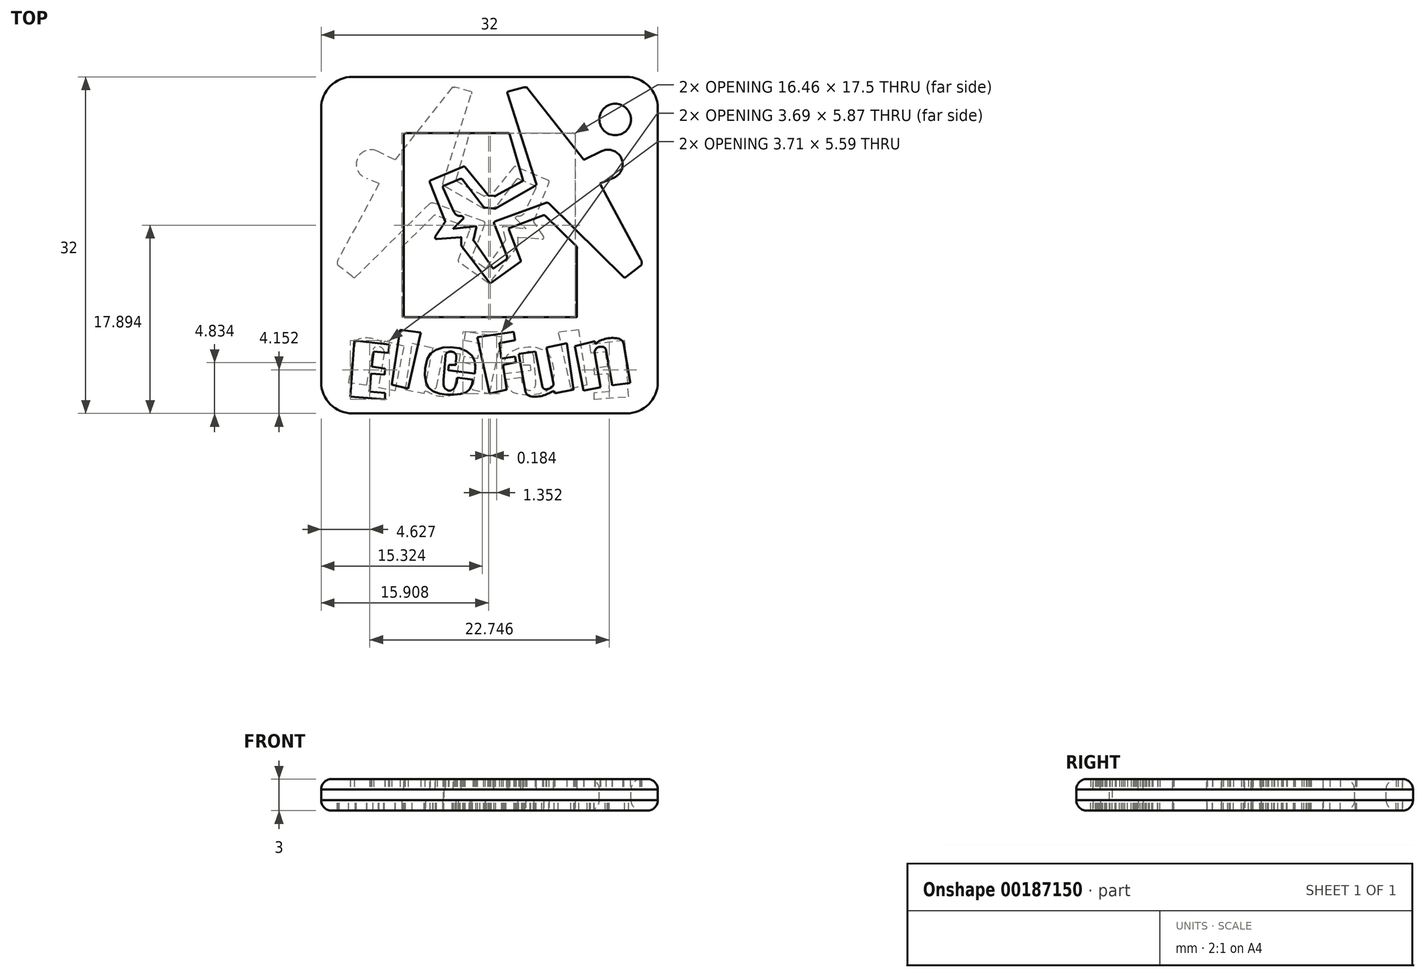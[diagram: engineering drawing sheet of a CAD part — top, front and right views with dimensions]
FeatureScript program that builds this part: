
annotation { "Feature Type Name" : "Feature", "Feature Type Description" : "" }
export const myFeature = defineFeature(function(context is Context, id is Id, definition is map)
    precondition{}
    {
        {
            var Q0;
            Q0=qCreatedBy(makeId("Top.planeOp"),FACE);
            var sketch = newSketch(context, id + "F0", { "sketchPlane" : qUnion([Q0])});
            skLineSegment(sketch, "E0", {"start": v(-15, 0) * mm, "end": v(15, 0) * mm, "construction": true});
            skLineSegment(sketch, "E1", {"start": v(0, 15) * mm, "end": v(0, 0) * mm, "construction": true});
            skLineSegment(sketch, "E2", {"start": v(0, 0) * mm, "end": v(0, -15) * mm, "construction": true});
            skLineSegment(sketch, "E3", {"start": v(1.86, 10.64) * mm, "end": v(-7.86, 10.64) * mm});
            skLineSegment(sketch, "E4", {"start": v(-8.14, 10.51) * mm, "end": v(-8.14, -6.7) * mm});
            skLineSegment(sketch, "E5", {"start": v(-8.02, -6.86) * mm, "end": v(8.23, -6.86) * mm});
            skLineSegment(sketch, "E6", {"start": v(8.32, -6.77) * mm, "end": v(8.32, -0.32) * mm});
            skLineSegment(sketch, "E7", {"start": v(8.28, -0.12) * mm, "end": v(5.28, 2.8) * mm});
            skLineSegment(sketch, "E8", {"start": v(1.92, 1.65) * mm, "end": v(5.12, 2.84) * mm});
            skLineSegment(sketch, "E9", {"start": v(1.74, 14.6) * mm, "end": v(3.24, 15) * mm});
            skLineSegment(sketch, "E10", {"start": v(3.55, 15) * mm, "end": v(8.98, 8.11) * mm});
            skLineSegment(sketch, "E11", {"start": v(8.98, 8.11) * mm, "end": v(10.65, 8.93) * mm});
            skLineSegment(sketch, "E12", {"start": v(10.49, 5.85) * mm, "end": v(11.64, 6.34) * mm});
            skLineSegment(sketch, "E13", {"start": v(10.49, 5.85) * mm, "end": v(14.37, -1.36) * mm});
            skLineSegment(sketch, "E14", {"start": v(13, -3.01) * mm, "end": v(14.27, -2.02) * mm});
            skLineSegment(sketch, "E15", {"start": v(12.74, -3.04) * mm, "end": v(5.65, 3.98) * mm});
            skLineSegment(sketch, "E16", {"start": v(0.54, 2.26) * mm, "end": v(5.35, 4.02) * mm});
            skLineSegment(sketch, "E17", {"start": v(0.45, 2.02) * mm, "end": v(1.66, -1.06) * mm});
            skLineSegment(sketch, "E18", {"start": v(2.97, -1.46) * mm, "end": v(1.87, 1.45) * mm});
            skLineSegment(sketch, "E19", {"start": v(0.4, -2.2) * mm, "end": v(1.6, -1.35) * mm});
            skLineSegment(sketch, "E20", {"start": v(0.28, -2.17) * mm, "end": v(-1.46, 0.35) * mm});
            skLineSegment(sketch, "E21", {"start": v(-1.52, 0.54) * mm, "end": v(-1.27, 1.67) * mm});
            skLineSegment(sketch, "E22", {"start": v(-1.33, 1.8) * mm, "end": v(-3.35, 1.58) * mm});
            skLineSegment(sketch, "E23", {"start": v(-2.43, 2.57) * mm, "end": v(-3.32, 1.7) * mm});
            skLineSegment(sketch, "E24", {"start": v(-2.43, 2.57) * mm, "end": v(-2.63, 2.76) * mm});
            skLineSegment(sketch, "E25", {"start": v(-4.4, 5.43) * mm, "end": v(-3.37, 3.16) * mm});
            skLineSegment(sketch, "E26", {"start": v(-2.79, 0.76) * mm, "end": v(-4.98, 0.6) * mm});
            skLineSegment(sketch, "E27", {"start": v(-5.16, 0.8) * mm, "end": v(-4.24, 2.18) * mm});
            skLineSegment(sketch, "E28", {"start": v(-4.24, 2.33) * mm, "end": v(-5.63, 5.88) * mm});
            skLineSegment(sketch, "E29", {"start": v(-5.63, 6.15) * mm, "end": v(-2.51, 7.46) * mm});
            skLineSegment(sketch, "E30", {"start": v(-2.34, 7.46) * mm, "end": v(-0.18, 4.8) * mm});
            skLineSegment(sketch, "E31", {"start": v(-0.07, 4.7) * mm, "end": v(0.46, 4.67) * mm});
            skLineSegment(sketch, "E32", {"start": v(0.57, 4.67) * mm, "end": v(3.12, 6.06) * mm});
            skLineSegment(sketch, "E33", {"start": v(3.16, 6.27) * mm, "end": v(1.9, 10.52) * mm});
            skLineSegment(sketch, "E34", {"start": v(0.1, -3.6) * mm, "end": v(2.9, -1.6) * mm});
            skLineSegment(sketch, "E35", {"start": v(-2.68, 0.7) * mm, "end": v(-2.7, 0.01) * mm});
            skLineSegment(sketch, "E36", {"start": v(-2.68, -0.05) * mm, "end": v(-0.03, -3.54) * mm});
            skLineSegment(sketch, "E37", {"start": v(-2.76, 6.3) * mm, "end": v(-4.36, 5.63) * mm});
            skLineSegment(sketch, "E38", {"start": v(-2.58, 6.26) * mm, "end": v(-0.6, 3.66) * mm});
            skLineSegment(sketch, "E39", {"start": v(-0.42, 3.58) * mm, "end": v(0.4, 3.49) * mm});
            skLineSegment(sketch, "E40", {"start": v(0.57, 3.49) * mm, "end": v(4.32, 5.63) * mm});
            skLineSegment(sketch, "E41", {"start": v(4.44, 5.9) * mm, "end": v(1.72, 14.38) * mm});
            skArc(sketch, "E42", {"start": v(11.64, 6.34) * mm, "mid": v(12.57, 8.18) * mm, "end": v(10.65, 8.93) * mm});
            skFitSpline(sketch, "E43", {"points": [v(1.74, 14.6) * mm, v(1.69, 14.5) * mm, v(1.72, 14.38) * mm], "startDerivative": vector(-0.14, -0.18) * mm, "endDerivative": vector(0.1, -0.25) * mm});
            skFitSpline(sketch, "E44", {"points": [v(3.24, 15) * mm, v(3.45, 15) * mm, v(3.55, 15) * mm], "startDerivative": vector(0.4, 0.05) * mm, "endDerivative": vector(0.21, -0.06) * mm});
            skFitSpline(sketch, "E45", {"points": [v(14.37, -1.36) * mm, v(14.45, -1.51) * mm, v(14.47, -1.68) * mm, v(14.44, -1.84) * mm, v(14.27, -2.02) * mm], "startDerivative": vector(0.37, -0.61) * mm, "endDerivative": vector(-0.7, -0.58) * mm});
            skFitSpline(sketch, "E46", {"points": [v(13, -3.01) * mm, v(12.88, -3.08) * mm, v(12.74, -3.04) * mm], "startDerivative": vector(-0.22, -0.18) * mm, "endDerivative": vector(-0.3, 0.12) * mm});
            skFitSpline(sketch, "E47", {"points": [v(5.65, 3.98) * mm, v(5.5, 4.03) * mm, v(5.35, 4.02) * mm], "startDerivative": vector(-0.3, 0.13) * mm, "endDerivative": vector(-0.3, -0.04) * mm});
            skArc(sketch, "E48", {"start": v(5.28, 2.8) * mm, "mid": v(5.2, 2.84) * mm, "end": v(5.12, 2.84) * mm});
            skFitSpline(sketch, "E49", {"points": [v(1.92, 1.65) * mm, v(1.86, 1.6) * mm, v(1.85, 1.55) * mm, v(1.87, 1.45) * mm], "startDerivative": vector(-0.21, -0.1) * mm, "endDerivative": vector(0.08, -0.26) * mm});
            skFitSpline(sketch, "E50", {"points": [v(2.97, -1.46) * mm, v(2.98, -1.5) * mm, v(2.97, -1.54) * mm, v(2.95, -1.57) * mm, v(2.9, -1.6) * mm], "startDerivative": vector(0.05, -0.15) * mm, "endDerivative": vector(-0.18, -0.1) * mm});
            skFitSpline(sketch, "E51", {"points": [v(1.66, -1.06) * mm, v(1.66, -1.2) * mm, v(1.6, -1.35) * mm], "startDerivative": vector(0.05, -0.3) * mm, "endDerivative": vector(-0.15, -0.27) * mm});
            skFitSpline(sketch, "E52", {"points": [v(0.4, -2.2) * mm, v(0.35, -2.2) * mm, v(0.28, -2.17) * mm], "startDerivative": vector(-0.13, -0.01) * mm, "endDerivative": vector(-0.12, 0.07) * mm});
            skArc(sketch, "E53", {"start": v(-1.52, 0.54) * mm, "mid": v(-1.52, 0.44) * mm, "end": v(-1.46, 0.35) * mm});
            skFitSpline(sketch, "E54", {"points": [v(-1.27, 1.67) * mm, v(-1.26, 1.7) * mm, v(-1.26, 1.75) * mm, v(-1.27, 1.77) * mm, v(-1.28, 1.79) * mm, v(-1.3, 1.8) * mm, v(-1.33, 1.8) * mm], "startDerivative": vector(0.06, 0.2) * mm, "endDerivative": vector(-0.18, -0.02) * mm});
            skFitSpline(sketch, "E55", {"points": [v(-3.32, 1.7) * mm, v(-3.4, 1.63) * mm, v(-3.44, 1.58) * mm, v(-3.43, 1.57) * mm, v(-3.4, 1.57) * mm, v(-3.35, 1.58) * mm], "startDerivative": vector(-0.28, -0.26) * mm, "endDerivative": vector(0.25, 0.03) * mm});
            skFitSpline(sketch, "E56", {"points": [v(-4.24, 2.18) * mm, v(-4.23, 2.2) * mm, v(-4.21, 2.23) * mm, v(-4.21, 2.25) * mm, v(-4.22, 2.28) * mm, v(-4.23, 2.31) * mm, v(-4.24, 2.33) * mm], "startDerivative": vector(0.05, 0.12) * mm, "endDerivative": vector(-0.05, 0.14) * mm});
            skFitSpline(sketch, "E57", {"points": [v(-2.63, 2.76) * mm, v(-2.75, 2.76) * mm, v(-2.87, 2.76) * mm, v(-3, 2.8) * mm, v(-3.15, 2.89) * mm, v(-3.26, 3) * mm, v(-3.37, 3.16) * mm], "startDerivative": vector(-0.82, 0.01) * mm, "endDerivative": vector(-0.6, 0.94) * mm});
            skFitSpline(sketch, "E58", {"points": [v(-4.4, 5.43) * mm, v(-4.44, 5.55) * mm, v(-4.36, 5.63) * mm], "startDerivative": vector(-0.14, 0.26) * mm, "endDerivative": vector(0.23, 0.16) * mm});
            skFitSpline(sketch, "E59", {"points": [v(-2.76, 6.3) * mm, v(-2.66, 6.3) * mm, v(-2.58, 6.26) * mm], "startDerivative": vector(0.22, 0.03) * mm, "endDerivative": vector(0.16, -0.12) * mm});
            skFitSpline(sketch, "E60", {"points": [v(-0.6, 3.66) * mm, v(-0.52, 3.6) * mm, v(-0.42, 3.58) * mm], "startDerivative": vector(0.15, -0.13) * mm, "endDerivative": vector(0.2, -0.02) * mm});
            skFitSpline(sketch, "E61", {"points": [v(0.4, 3.49) * mm, v(0.5, 3.49) * mm, v(0.57, 3.49) * mm], "startDerivative": vector(0.17, 0) * mm, "endDerivative": vector(0.15, 0) * mm});
            skFitSpline(sketch, "E62", {"points": [v(0.57, 4.67) * mm, v(0.54, 4.66) * mm, v(0.46, 4.67) * mm], "startDerivative": vector(-0.06, -0.02) * mm, "endDerivative": vector(-0.15, 0.02) * mm});
            skFitSpline(sketch, "E63", {"points": [v(-0.07, 4.7) * mm, v(-0.12, 4.73) * mm, v(-0.18, 4.8) * mm], "startDerivative": vector(-0.12, 0.05) * mm, "endDerivative": vector(-0.1, 0.13) * mm});
            skFitSpline(sketch, "E64", {"points": [v(-8.14, 10.51) * mm, v(-8.07, 10.6) * mm, v(-7.95, 10.64) * mm, v(-7.86, 10.64) * mm], "startDerivative": vector(0.18, 0.27) * mm, "endDerivative": vector(0.29, 0) * mm});
            skFitSpline(sketch, "E65", {"points": [v(1.9, 10.52) * mm, v(1.88, 10.6) * mm, v(1.86, 10.64) * mm], "startDerivative": vector(-0.05, 0.15) * mm, "endDerivative": vector(-0.04, 0.1) * mm});
            skFitSpline(sketch, "E66", {"points": [v(4.44, 5.9) * mm, v(4.45, 5.84) * mm, v(4.45, 5.77) * mm, v(4.43, 5.72) * mm, v(4.4, 5.69) * mm, v(4.32, 5.63) * mm], "startDerivative": vector(0.07, -0.32) * mm, "endDerivative": vector(-0.37, -0.23) * mm});
            skFitSpline(sketch, "E67", {"points": [v(3.12, 6.06) * mm, v(3.16, 6.1) * mm, v(3.18, 6.13) * mm, v(3.18, 6.17) * mm, v(3.16, 6.27) * mm], "startDerivative": vector(0.2, 0.13) * mm, "endDerivative": vector(-0.1, 0.32) * mm});
            skFitSpline(sketch, "E68", {"points": [v(-4.98, 0.6) * mm, v(-5.04, 0.6) * mm, v(-5.1, 0.6) * mm, v(-5.13, 0.63) * mm, v(-5.16, 0.66) * mm, v(-5.17, 0.7) * mm, v(-5.17, 0.74) * mm, v(-5.17, 0.78) * mm, v(-5.16, 0.8) * mm], "startDerivative": vector(-0.4, 0) * mm, "endDerivative": vector(0.04, 0.24) * mm});
            skFitSpline(sketch, "E69", {"points": [v(-2.68, 0.7) * mm, v(-2.68, 0.73) * mm, v(-2.69, 0.74) * mm, v(-2.7, 0.75) * mm, v(-2.72, 0.76) * mm, v(-2.74, 0.76) * mm, v(-2.79, 0.76) * mm], "startDerivative": vector(-0.02, 0.12) * mm, "endDerivative": vector(-0.22, -0.02) * mm});
            skFitSpline(sketch, "E70", {"points": [v(-2.68, -0.05) * mm, v(-2.7, -0.03) * mm, v(-2.7, 0.01) * mm], "startDerivative": vector(-0.02, 0.05) * mm, "endDerivative": vector(0, 0.08) * mm});
            skFitSpline(sketch, "E71", {"points": [v(0.1, -3.6) * mm, v(0.08, -3.6) * mm, v(0.04, -3.6) * mm, v(0, -3.6) * mm, v(-0.03, -3.54) * mm], "startDerivative": vector(-0.1, -0.1) * mm, "endDerivative": vector(-0.12, 0.19) * mm});
            skFitSpline(sketch, "E72", {"points": [v(-8.14, -6.7) * mm, v(-8.14, -6.74) * mm, v(-8.13, -6.78) * mm, v(-8.1, -6.82) * mm, v(-8.08, -6.84) * mm, v(-8.04, -6.86) * mm, v(-8.02, -6.86) * mm], "startDerivative": vector(-0.01, -0.18) * mm, "endDerivative": vector(0.15, 0.01) * mm});
            skFitSpline(sketch, "E73", {"points": [v(8.32, -6.77) * mm, v(8.3, -6.83) * mm, v(8.23, -6.86) * mm], "startDerivative": vector(-0.01, -0.15) * mm, "endDerivative": vector(-0.16, -0.02) * mm});
            skFitSpline(sketch, "E74", {"points": [v(8.32, -0.32) * mm, v(8.32, -0.22) * mm, v(8.28, -0.12) * mm], "startDerivative": vector(0.02, 0.2) * mm, "endDerivative": vector(-0.1, 0.2) * mm});
            skFitSpline(sketch, "E75", {"points": [v(-5.63, 5.88) * mm, v(-5.68, 6.02) * mm, v(-5.63, 6.15) * mm], "startDerivative": vector(-0.15, 0.28) * mm, "endDerivative": vector(0.15, 0.27) * mm});
            skFitSpline(sketch, "E76", {"points": [v(-2.51, 7.46) * mm, v(-2.42, 7.48) * mm, v(-2.34, 7.46) * mm], "startDerivative": vector(0.18, 0.06) * mm, "endDerivative": vector(0.15, -0.07) * mm});
            skLineSegment(sketch, "E77", {"start": v(-9.52, -9.44) * mm, "end": v(-9.6, -10.25) * mm});
            skLineSegment(sketch, "E78", {"start": v(-9.6, -10.25) * mm, "end": v(-11, -10.11) * mm});
            skLineSegment(sketch, "E79", {"start": v(-11, -10.11) * mm, "end": v(-11.2, -11.55) * mm});
            skLineSegment(sketch, "E80", {"start": v(-11.2, -11.55) * mm, "end": v(-9.91, -11.72) * mm});
            skLineSegment(sketch, "E81", {"start": v(-9.91, -11.72) * mm, "end": v(-9.96, -12.3) * mm});
            skLineSegment(sketch, "E82", {"start": v(-9.96, -12.3) * mm, "end": v(-11.25, -12.2) * mm});
            skLineSegment(sketch, "E83", {"start": v(-11.25, -12.2) * mm, "end": v(-11.4, -13.92) * mm});
            skLineSegment(sketch, "E84", {"start": v(-11.4, -13.92) * mm, "end": v(-9.9, -14.05) * mm});
            skLineSegment(sketch, "E85", {"start": v(-9.9, -14.05) * mm, "end": v(-9.9, -14.64) * mm});
            skLineSegment(sketch, "E86", {"start": v(-9.9, -14.64) * mm, "end": v(-13.23, -14.4) * mm});
            skLineSegment(sketch, "E87", {"start": v(-13.23, -14.4) * mm, "end": v(-12.84, -9.05) * mm});
            skLineSegment(sketch, "E88", {"start": v(-12.84, -9.05) * mm, "end": v(-9.52, -9.44) * mm});
            skLineSegment(sketch, "E89", {"start": v(-8.48, -8.05) * mm, "end": v(-6.54, -8.29) * mm});
            skLineSegment(sketch, "E90", {"start": v(-6.54, -8.29) * mm, "end": v(-7.72, -13.63) * mm});
            skLineSegment(sketch, "E91", {"start": v(-7.72, -13.63) * mm, "end": v(-9.28, -13.26) * mm});
            skLineSegment(sketch, "E92", {"start": v(-9.28, -13.26) * mm, "end": v(-8.48, -8.05) * mm});
            skLineSegment(sketch, "E93", {"start": v(-3.17, -10.43) * mm, "end": v(-3.2, -11.4) * mm});
            skLineSegment(sketch, "E94", {"start": v(-3.2, -11.4) * mm, "end": v(-3.87, -11.4) * mm});
            skFitSpline(sketch, "E95", {"points": [v(-4.2, -10.53) * mm, v(-4.15, -10.37) * mm, v(-4.02, -10.22) * mm, v(-3.84, -10.13) * mm, v(-3.58, -10.13) * mm, v(-3.37, -10.2) * mm, v(-3.24, -10.32) * mm, v(-3.17, -10.43) * mm], "startDerivative": vector(0.24, 1.24) * mm, "endDerivative": vector(0.53, -0.96) * mm});
            skLineSegment(sketch, "E96", {"start": v(-1.38, -12.22) * mm, "end": v(-3.93, -11.9) * mm});
            skLineSegment(sketch, "E97", {"start": v(-3.06, -12.6) * mm, "end": v(-1.58, -12.8) * mm});
            skFitSpline(sketch, "E98", {"points": [v(-1.58, -12.8) * mm, v(-1.61, -13.06) * mm, v(-1.68, -13.28) * mm, v(-1.78, -13.5) * mm, v(-1.9, -13.7) * mm, v(-2.08, -13.9) * mm, v(-2.35, -14.05) * mm, v(-2.72, -14.14) * mm, v(-3.17, -14.2) * mm, v(-3.7, -14.2) * mm, v(-4.27, -14.19) * mm, v(-4.76, -14.11) * mm, v(-5.25, -13.94) * mm, v(-5.5, -13.78) * mm, v(-5.75, -13.59) * mm, v(-5.94, -13.25) * mm, v(-6.09, -12.8) * mm, v(-6.14, -12.22) * mm, v(-6.12, -11.7) * mm, v(-5.92, -10.84) * mm, v(-5.69, -10.42) * mm, v(-5.37, -10.12) * mm, v(-4.96, -9.9) * mm, v(-4.42, -9.73) * mm, v(-3.73, -9.7) * mm, v(-2.96, -9.77) * mm, v(-2.33, -9.98) * mm, v(-1.87, -10.28) * mm, v(-1.58, -10.62) * mm, v(-1.4, -10.98) * mm, v(-1.35, -11.33) * mm, v(-1.34, -11.71) * mm, v(-1.38, -12.22) * mm], "startDerivative": vector(-0.95, -11.32) * mm, "endDerivative": vector(-1.59, -15.64) * mm});
            skLineSegment(sketch, "E99", {"start": v(1.62, -13.75) * mm, "end": v(0, -14.1) * mm});
            skLineSegment(sketch, "E100", {"start": v(0, -14.1) * mm, "end": v(-1.17, -8.73) * mm});
            skLineSegment(sketch, "E101", {"start": v(-1.17, -8.73) * mm, "end": v(2.3, -8.23) * mm});
            skLineSegment(sketch, "E102", {"start": v(2.3, -8.23) * mm, "end": v(2.42, -9.03) * mm});
            skLineSegment(sketch, "E103", {"start": v(2.42, -9.03) * mm, "end": v(0.92, -9.32) * mm});
            skLineSegment(sketch, "E104", {"start": v(0.92, -9.32) * mm, "end": v(1.14, -10.78) * mm});
            skLineSegment(sketch, "E105", {"start": v(1.14, -10.78) * mm, "end": v(2.44, -10.6) * mm});
            skLineSegment(sketch, "E106", {"start": v(2.44, -10.6) * mm, "end": v(2.52, -11.14) * mm});
            skLineSegment(sketch, "E107", {"start": v(2.52, -11.14) * mm, "end": v(1.28, -11.38) * mm});
            skLineSegment(sketch, "E108", {"start": v(1.28, -11.38) * mm, "end": v(1.62, -13.75) * mm});
            skLineSegment(sketch, "E109", {"start": v(7.98, -13.75) * mm, "end": v(6.2, -14.08) * mm});
            skLineSegment(sketch, "E110", {"start": v(6.2, -14.08) * mm, "end": v(6.13, -13.86) * mm});
            skLineSegment(sketch, "E111", {"start": v(7.98, -13.75) * mm, "end": v(7.34, -9.32) * mm});
            skLineSegment(sketch, "E112", {"start": v(7.34, -9.32) * mm, "end": v(5.4, -9.74) * mm});
            skLineSegment(sketch, "E113", {"start": v(5.4, -9.74) * mm, "end": v(6.08, -13.15) * mm});
            skLineSegment(sketch, "E114", {"start": v(5.02, -13.5) * mm, "end": v(4.37, -10.12) * mm});
            skLineSegment(sketch, "E115", {"start": v(4.37, -10.12) * mm, "end": v(2.77, -10.33) * mm});
            skLineSegment(sketch, "E116", {"start": v(2.77, -10.33) * mm, "end": v(3.4, -13.9) * mm});
            skFitSpline(sketch, "E117", {"points": [v(3.4, -13.9) * mm, v(3.49, -14.1) * mm, v(3.68, -14.27) * mm, v(3.94, -14.38) * mm, v(4.27, -14.4) * mm, v(4.69, -14.38) * mm, v(5.07, -14.3) * mm, v(5.38, -14.2) * mm, v(5.68, -14.07) * mm, v(5.87, -13.97) * mm, v(6, -13.9) * mm, v(6.13, -13.86) * mm], "startDerivative": vector(0.77, -2.56) * mm, "endDerivative": vector(2.11, 0.24) * mm});
            skFitSpline(sketch, "E118", {"points": [v(6.08, -13.15) * mm, v(6.08, -13.3) * mm, v(5.99, -13.43) * mm, v(5.86, -13.54) * mm, v(5.67, -13.64) * mm, v(5.51, -13.68) * mm, v(5.33, -13.7) * mm, v(5.2, -13.66) * mm, v(5.11, -13.6) * mm, v(5.02, -13.5) * mm], "startDerivative": vector(0.2, -1.45) * mm, "endDerivative": vector(-0.8, 1.2) * mm});
            skLineSegment(sketch, "E119", {"start": v(10.55, -13.52) * mm, "end": v(8.95, -13.82) * mm});
            skLineSegment(sketch, "E120", {"start": v(8.95, -13.82) * mm, "end": v(8.1, -9.6) * mm});
            skLineSegment(sketch, "E121", {"start": v(8.1, -9.6) * mm, "end": v(10.02, -9.13) * mm});
            skLineSegment(sketch, "E122", {"start": v(10.02, -9.13) * mm, "end": v(10.05, -9.43) * mm});
            skLineSegment(sketch, "E123", {"start": v(9.98, -10.17) * mm, "end": v(10.55, -13.52) * mm});
            skLineSegment(sketch, "E124", {"start": v(11.66, -13.3) * mm, "end": v(11.06, -9.93) * mm});
            skLineSegment(sketch, "E125", {"start": v(11.66, -13.3) * mm, "end": v(13.38, -13.1) * mm});
            skLineSegment(sketch, "E126", {"start": v(13.38, -13.1) * mm, "end": v(12.75, -9.36) * mm});
            skPoint(sketch, "E127.1.internal.snap0", {"position": v(10.04, -9.28) * mm});
            skFitSpline(sketch, "E127", {"points": [v(9.98, -10.17) * mm, v(10.04, -9.98) * mm, v(10.15, -9.81) * mm, v(10.35, -9.7) * mm, v(10.58, -9.65) * mm, v(10.8, -9.68) * mm, v(10.92, -9.73) * mm, v(11, -9.8) * mm, v(11.06, -9.93) * mm], "startDerivative": vector(0.35, 1.5) * mm, "endDerivative": vector(0.4, -1.27) * mm});
            skFitSpline(sketch, "E128", {"points": [v(10.05, -9.43) * mm, v(10.22, -9.26) * mm, v(10.4, -9.14) * mm, v(10.7, -9) * mm, v(11.1, -8.88) * mm, v(11.5, -8.83) * mm, v(11.9, -8.84) * mm, v(12.26, -8.88) * mm, v(12.5, -8.98) * mm, v(12.65, -9.13) * mm, v(12.7, -9.24) * mm, v(12.75, -9.36) * mm], "startDerivative": vector(2, 2.1) * mm, "endDerivative": vector(0.8, -1.94) * mm});
            skFitSpline(sketch, "E129", {"points": [v(-4.1, -11.87) * mm, v(-4.2, -12.04) * mm, v(-4.27, -12.28) * mm, v(-4.35, -12.58) * mm, v(-4.37, -12.86) * mm, v(-4.38, -13.16) * mm, v(-4.32, -13.48) * mm, v(-4.14, -13.7) * mm, v(-3.92, -13.8) * mm, v(-3.7, -13.82) * mm, v(-3.5, -13.73) * mm, v(-3.35, -13.58) * mm, v(-3.22, -13.37) * mm, v(-3.14, -13.13) * mm, v(-3.1, -12.91) * mm, v(-3.06, -12.6) * mm], "startDerivative": vector(-1.74, -2.77) * mm, "endDerivative": vector(0.4, 4.42) * mm});
            skFitSpline(sketch, "E130", {"points": [v(0.45, 2.02) * mm, v(0.43, 2.1) * mm, v(0.45, 2.18) * mm, v(0.54, 2.26) * mm], "startDerivative": vector(-0.1, 0.25) * mm, "endDerivative": vector(0.3, 0.19) * mm});
            skLineSegment(sketch, "E131", {"start": v(8.89, 15) * mm, "end": v(15, 8.89) * mm, "construction": true});
            skCircle(sketch, "E132", {"center": v(11.94, 11.94) * mm, "radius": 1.5 * mm});
            skLineSegment(sketch, "E133.bottom", {"start": v(-13, 16) * mm, "end": v(13, 16) * mm});
            skLineSegment(sketch, "E133.top", {"start": v(-13, -16) * mm, "end": v(13, -16) * mm});
            skLineSegment(sketch, "E133.left", {"start": v(-16, 13) * mm, "end": v(-16, -13) * mm});
            skLineSegment(sketch, "E133.right", {"start": v(16, 13) * mm, "end": v(16, -13) * mm});
            skLineSegment(sketch, "E134", {"start": v(-16, 0) * mm, "end": v(16, 0) * mm, "construction": true});
            skLineSegment(sketch, "E135", {"start": v(0, 16) * mm, "end": v(0, -16) * mm, "construction": true});
            skLineSegment(sketch, "E136", {"start": v(0, 0) * mm, "end": v(0, -16) * mm, "construction": true});
            skLineSegment(sketch, "E137", {"start": v(0, -16) * mm, "end": v(0, 0) * mm, "construction": true});
            skLineSegment(sketch, "E138", {"start": v(0, 16) * mm, "end": v(0, 0) * mm, "construction": true});
            skPoint(sketch, "E139.visualSharp", {"position": v(-16, 16) * mm});
            skArc(sketch, "E139.filletArc", {"start": v(-13, 16) * mm, "mid": v(-15.12, 15.12) * mm, "end": v(-16, 13) * mm});
            skPoint(sketch, "E140.visualSharp", {"position": v(16, 16) * mm});
            skArc(sketch, "E140.filletArc", {"start": v(16, 13) * mm, "mid": v(15.12, 15.12) * mm, "end": v(13, 16) * mm});
            skPoint(sketch, "E141.visualSharp", {"position": v(16, -16) * mm});
            skArc(sketch, "E141.filletArc", {"start": v(13, -16) * mm, "mid": v(15.12, -15.12) * mm, "end": v(16, -13) * mm});
            skPoint(sketch, "E142.visualSharp", {"position": v(-16, -16) * mm});
            skArc(sketch, "E142.filletArc", {"start": v(-16, -13) * mm, "mid": v(-15.12, -15.12) * mm, "end": v(-13, -16) * mm});
            skLineSegment(sketch, "E143", {"start": v(-4.19, -10.48) * mm, "end": v(-4.37, -12.86) * mm});
            skLineSegment(sketch, "E144", {"start": v(-3.87, -11.4) * mm, "end": v(-3.93, -11.9) * mm});
            skSolve(sketch);
        }
        {
            var Q0;
            Q0=makeQuery(id+"F0.imprint","IMPRINT",FACE,{"disambiguationData":[TD([[makeQuery(id+"F0.imprint","IMPRINT",EDGE,{"derivedFrom":sQuery(id+"F0.wireOp",EDGE,"E9")}),-1.0]])]});
            var Q1;
            Q1=makeQuery(id+"F0.imprint","IMPRINT",FACE,{"disambiguationData":[TD([[makeQuery(id+"F0.imprint","IMPRINT",EDGE,{"derivedFrom":sQuery(id+"F0.wireOp",EDGE,"E132")}),1.0]])]});
            var Q2;
            Q2=makeQuery(id+"F0.imprint","IMPRINT",FACE,{"disambiguationData":[TD([[makeQuery(id+"F0.imprint","IMPRINT",EDGE,{"derivedFrom":sQuery(id+"F0.wireOp",EDGE,"E119")}),-1.0]])]});
            var Q3;
            Q3=makeQuery(id+"F0.imprint","IMPRINT",FACE,{"disambiguationData":[TD([[makeQuery(id+"F0.imprint","IMPRINT",EDGE,{"derivedFrom":sQuery(id+"F0.wireOp",EDGE,"E93")}),1.0]])]});
            var Q4;
            Q4=makeQuery(id+"F0.imprint","IMPRINT",FACE,{"disambiguationData":[TD([[makeQuery(id+"F0.imprint","IMPRINT",EDGE,{"derivedFrom":sQuery(id+"F0.wireOp",EDGE,"E3")}),1.0]])]});
            var Q5;
            Q5=makeQuery(id+"F0.imprint","IMPRINT",FACE,{"disambiguationData":[TD([[makeQuery(id+"F0.imprint","IMPRINT",EDGE,{"derivedFrom":sQuery(id+"F0.wireOp",EDGE,"E3")}),-1.0]])]});
            var Q6;
            Q6=makeQuery(id+"F0.imprint","IMPRINT",FACE,{"disambiguationData":[TD([[makeQuery(id+"F0.imprint","IMPRINT",EDGE,{"derivedFrom":sQuery(id+"F0.wireOp",EDGE,"E89")}),-1.0]])]});
            var Q7;
            Q7=makeQuery(id+"F0.imprint","IMPRINT",FACE,{"disambiguationData":[TD([[makeQuery(id+"F0.imprint","IMPRINT",EDGE,{"derivedFrom":sQuery(id+"F0.wireOp",EDGE,"E99")}),-1.0]])]});
            var Q8;
            Q8=makeQuery(id+"F0.imprint","IMPRINT",FACE,{"disambiguationData":[TD([[makeQuery(id+"F0.imprint","IMPRINT",EDGE,{"derivedFrom":sQuery(id+"F0.wireOp",EDGE,"E109")}),-1.0]])]});
            var Q9;
            Q9=makeQuery(id+"F0.imprint","IMPRINT",FACE,{"disambiguationData":[TD([[makeQuery(id+"F0.imprint","IMPRINT",EDGE,{"derivedFrom":sQuery(id+"F0.wireOp",EDGE,"E77")}),-1.0]])]});
            extrude(context, id + "F1", {"entities" : qUnion([Q0, Q1, Q2, Q3, Q4, Q5, Q6, Q7, Q8, Q9]), "oppositeDirection" : true, "depth" : 1 * mm});
        }
        {
            var Q0;
            Q0=makeQuery(id+"F0.imprint","IMPRINT",FACE,{"disambiguationData":[TD([[makeQuery(id+"F0.imprint","IMPRINT",EDGE,{"derivedFrom":sQuery(id+"F0.wireOp",EDGE,"E3")}),-1.0]])]});
            extrude(context, id + "F2", {"entities" : qUnion([Q0]), "depth" : 1 * mm});
        }
        {
            var Q0;
            Q0=makeQuery(id+"F1.opExtrude","CAP_FACE",FACE,{"disambiguationData":[OSD([sQuery(id+"F0.wireOp",EDGE,"E133.bottom"),sQuery(id+"F0.wireOp",EDGE,"E133.top"),sQuery(id+"F0.wireOp",EDGE,"E133.left"),sQuery(id+"F0.wireOp",EDGE,"E133.right"),sQuery(id+"F0.wireOp",EDGE,"E139.filletArc"),sQuery(id+"F0.wireOp",EDGE,"E140.filletArc"),sQuery(id+"F0.wireOp",EDGE,"E141.filletArc"),sQuery(id+"F0.wireOp",EDGE,"E142.filletArc")])],"isStart":false});
            var sketch = newSketch(context, id + "F3", { "sketchPlane" : qUnion([Q0])});
            skLineSegment(sketch, "E145", {"start": v(-15.73, 2.68) * mm, "end": v(14.27, 2.68) * mm, "construction": true});
            skLineSegment(sketch, "E146", {"start": v(-0.73, 17.68) * mm, "end": v(-0.73, 2.68) * mm, "construction": true});
            skLineSegment(sketch, "E147", {"start": v(-0.73, 2.68) * mm, "end": v(-0.73, -12.32) * mm, "construction": true});
            skLineSegment(sketch, "E148", {"start": v(1.13, 13.33) * mm, "end": v(-8.59, 13.33) * mm});
            skLineSegment(sketch, "E149", {"start": v(-8.87, 13.2) * mm, "end": v(-8.87, -4.03) * mm});
            skLineSegment(sketch, "E150", {"start": v(-8.75, -4.17) * mm, "end": v(7.5, -4.17) * mm});
            skLineSegment(sketch, "E151", {"start": v(7.58, -4.09) * mm, "end": v(7.58, 2.37) * mm});
            skLineSegment(sketch, "E152", {"start": v(7.54, 2.56) * mm, "end": v(4.54, 5.48) * mm});
            skLineSegment(sketch, "E153", {"start": v(1.19, 4.33) * mm, "end": v(4.4, 5.53) * mm});
            skLineSegment(sketch, "E154", {"start": v(1, 17.28) * mm, "end": v(2.5, 17.67) * mm});
            skLineSegment(sketch, "E155", {"start": v(2.82, 17.67) * mm, "end": v(8.25, 10.8) * mm});
            skLineSegment(sketch, "E156", {"start": v(8.25, 10.8) * mm, "end": v(9.91, 11.61) * mm});
            skLineSegment(sketch, "E157", {"start": v(9.75, 8.54) * mm, "end": v(10.9, 9.02) * mm});
            skLineSegment(sketch, "E158", {"start": v(9.75, 8.54) * mm, "end": v(13.64, 1.32) * mm});
            skLineSegment(sketch, "E159", {"start": v(12.27, -0.33) * mm, "end": v(13.54, 0.67) * mm});
            skLineSegment(sketch, "E160", {"start": v(12, -0.36) * mm, "end": v(4.92, 6.66) * mm});
            skLineSegment(sketch, "E161", {"start": v(-0.19, 4.94) * mm, "end": v(4.62, 6.7) * mm});
            skLineSegment(sketch, "E162", {"start": v(-0.28, 4.7) * mm, "end": v(0.92, 1.62) * mm});
            skLineSegment(sketch, "E163", {"start": v(2.24, 1.22) * mm, "end": v(1.13, 4.14) * mm});
            skLineSegment(sketch, "E164", {"start": v(-0.33, 0.48) * mm, "end": v(0.87, 1.33) * mm});
            skLineSegment(sketch, "E165", {"start": v(-0.45, 0.51) * mm, "end": v(-2.2, 3.04) * mm});
            skLineSegment(sketch, "E166", {"start": v(-2.26, 3.23) * mm, "end": v(-2, 4.35) * mm});
            skLineSegment(sketch, "E167", {"start": v(-2.06, 4.48) * mm, "end": v(-4.08, 4.26) * mm});
            skLineSegment(sketch, "E168", {"start": v(-3.16, 5.25) * mm, "end": v(-4.06, 4.39) * mm});
            skLineSegment(sketch, "E169", {"start": v(-3.16, 5.25) * mm, "end": v(-3.36, 5.45) * mm});
            skLineSegment(sketch, "E170", {"start": v(-5.13, 8.1) * mm, "end": v(-4.1, 5.85) * mm});
            skLineSegment(sketch, "E171", {"start": v(-3.52, 3.44) * mm, "end": v(-5.71, 3.28) * mm});
            skLineSegment(sketch, "E172", {"start": v(-5.9, 3.48) * mm, "end": v(-4.97, 4.86) * mm});
            skLineSegment(sketch, "E173", {"start": v(-4.97, 5.02) * mm, "end": v(-6.36, 8.56) * mm});
            skLineSegment(sketch, "E174", {"start": v(-6.36, 8.84) * mm, "end": v(-3.24, 10.14) * mm});
            skLineSegment(sketch, "E175", {"start": v(-3.08, 10.14) * mm, "end": v(-0.91, 7.48) * mm});
            skLineSegment(sketch, "E176", {"start": v(-0.8, 7.39) * mm, "end": v(-0.27, 7.35) * mm});
            skLineSegment(sketch, "E177", {"start": v(-0.16, 7.35) * mm, "end": v(2.39, 8.75) * mm});
            skLineSegment(sketch, "E178", {"start": v(2.43, 8.95) * mm, "end": v(1.18, 13.2) * mm});
            skLineSegment(sketch, "E179", {"start": v(-0.63, -0.9) * mm, "end": v(2.17, 1.08) * mm});
            skLineSegment(sketch, "E180", {"start": v(-3.4, 3.4) * mm, "end": v(-3.42, 2.7) * mm});
            skLineSegment(sketch, "E181", {"start": v(-3.42, 2.63) * mm, "end": v(-0.76, -0.86) * mm});
            skLineSegment(sketch, "E182", {"start": v(-3.5, 8.99) * mm, "end": v(-5.09, 8.32) * mm});
            skLineSegment(sketch, "E183", {"start": v(-3.3, 8.94) * mm, "end": v(-1.33, 6.34) * mm});
            skLineSegment(sketch, "E184", {"start": v(-1.15, 6.26) * mm, "end": v(-0.32, 6.17) * mm});
            skLineSegment(sketch, "E185", {"start": v(-0.16, 6.17) * mm, "end": v(3.59, 8.32) * mm});
            skLineSegment(sketch, "E186", {"start": v(3.7, 8.58) * mm, "end": v(0.99, 17.06) * mm});
            skArc(sketch, "E187", {"start": v(10.9, 9.02) * mm, "mid": v(11.84, 10.86) * mm, "end": v(9.91, 11.61) * mm});
            skFitSpline(sketch, "E188", {"points": [v(1, 17.28) * mm, v(0.96, 17.19) * mm, v(0.99, 17.06) * mm], "startDerivative": vector(-0.14, -0.18) * mm, "endDerivative": vector(0.1, -0.25) * mm});
            skFitSpline(sketch, "E189", {"points": [v(2.5, 17.67) * mm, v(2.72, 17.7) * mm, v(2.82, 17.67) * mm], "startDerivative": vector(0.4, 0.05) * mm, "endDerivative": vector(0.21, -0.06) * mm});
            skFitSpline(sketch, "E190", {"points": [v(13.64, 1.32) * mm, v(13.72, 1.17) * mm, v(13.74, 1) * mm, v(13.71, 0.84) * mm, v(13.54, 0.67) * mm], "startDerivative": vector(0.37, -0.61) * mm, "endDerivative": vector(-0.7, -0.58) * mm});
            skFitSpline(sketch, "E191", {"points": [v(12.27, -0.33) * mm, v(12.15, -0.4) * mm, v(12, -0.36) * mm], "startDerivative": vector(-0.22, -0.18) * mm, "endDerivative": vector(-0.3, 0.12) * mm});
            skFitSpline(sketch, "E192", {"points": [v(4.92, 6.66) * mm, v(4.77, 6.71) * mm, v(4.62, 6.7) * mm], "startDerivative": vector(-0.3, 0.13) * mm, "endDerivative": vector(-0.3, -0.04) * mm});
            skArc(sketch, "E193", {"start": v(4.54, 5.48) * mm, "mid": v(4.47, 5.52) * mm, "end": v(4.4, 5.53) * mm});
            skFitSpline(sketch, "E194", {"points": [v(1.19, 4.33) * mm, v(1.13, 4.3) * mm, v(1.11, 4.23) * mm, v(1.13, 4.14) * mm], "startDerivative": vector(-0.21, -0.1) * mm, "endDerivative": vector(0.08, -0.26) * mm});
            skFitSpline(sketch, "E195", {"points": [v(2.24, 1.22) * mm, v(2.25, 1.19) * mm, v(2.24, 1.15) * mm, v(2.22, 1.1) * mm, v(2.17, 1.08) * mm], "startDerivative": vector(0.05, -0.15) * mm, "endDerivative": vector(-0.18, -0.1) * mm});
            skFitSpline(sketch, "E196", {"points": [v(0.92, 1.62) * mm, v(0.93, 1.47) * mm, v(0.87, 1.33) * mm], "startDerivative": vector(0.05, -0.3) * mm, "endDerivative": vector(-0.15, -0.27) * mm});
            skFitSpline(sketch, "E197", {"points": [v(-0.33, 0.48) * mm, v(-0.39, 0.48) * mm, v(-0.45, 0.51) * mm], "startDerivative": vector(-0.13, -0.01) * mm, "endDerivative": vector(-0.12, 0.07) * mm});
            skArc(sketch, "E198", {"start": v(-2.26, 3.23) * mm, "mid": v(-2.25, 3.12) * mm, "end": v(-2.2, 3.04) * mm});
            skFitSpline(sketch, "E199", {"points": [v(-2, 4.35) * mm, v(-2, 4.4) * mm, v(-2, 4.43) * mm, v(-2, 4.45) * mm, v(-2.01, 4.47) * mm, v(-2.03, 4.48) * mm, v(-2.06, 4.48) * mm], "startDerivative": vector(0.06, 0.2) * mm, "endDerivative": vector(-0.18, -0.02) * mm});
            skFitSpline(sketch, "E200", {"points": [v(-4.06, 4.39) * mm, v(-4.14, 4.31) * mm, v(-4.17, 4.27) * mm, v(-4.16, 4.25) * mm, v(-4.13, 4.25) * mm, v(-4.08, 4.26) * mm], "startDerivative": vector(-0.28, -0.26) * mm, "endDerivative": vector(0.25, 0.03) * mm});
            skFitSpline(sketch, "E201", {"points": [v(-4.97, 4.86) * mm, v(-4.96, 4.88) * mm, v(-4.95, 4.9) * mm, v(-4.95, 4.93) * mm, v(-4.95, 4.97) * mm, v(-4.96, 5) * mm, v(-4.97, 5.02) * mm], "startDerivative": vector(0.05, 0.12) * mm, "endDerivative": vector(-0.05, 0.14) * mm});
            skFitSpline(sketch, "E202", {"points": [v(-3.36, 5.45) * mm, v(-3.48, 5.45) * mm, v(-3.6, 5.45) * mm, v(-3.73, 5.49) * mm, v(-3.88, 5.57) * mm, v(-4, 5.67) * mm, v(-4.1, 5.85) * mm], "startDerivative": vector(-0.82, 0.01) * mm, "endDerivative": vector(-0.6, 0.94) * mm});
            skFitSpline(sketch, "E203", {"points": [v(-5.13, 8.1) * mm, v(-5.17, 8.23) * mm, v(-5.09, 8.32) * mm], "startDerivative": vector(-0.14, 0.26) * mm, "endDerivative": vector(0.23, 0.16) * mm});
            skFitSpline(sketch, "E204", {"points": [v(-3.5, 8.99) * mm, v(-3.39, 8.99) * mm, v(-3.3, 8.94) * mm], "startDerivative": vector(0.22, 0.03) * mm, "endDerivative": vector(0.16, -0.12) * mm});
            skFitSpline(sketch, "E205", {"points": [v(-1.33, 6.34) * mm, v(-1.25, 6.28) * mm, v(-1.15, 6.26) * mm], "startDerivative": vector(0.15, -0.13) * mm, "endDerivative": vector(0.2, -0.02) * mm});
            skFitSpline(sketch, "E206", {"points": [v(-0.32, 6.17) * mm, v(-0.24, 6.17) * mm, v(-0.16, 6.17) * mm], "startDerivative": vector(0.17, 0) * mm, "endDerivative": vector(0.15, 0) * mm});
            skFitSpline(sketch, "E207", {"points": [v(-0.16, 7.35) * mm, v(-0.19, 7.34) * mm, v(-0.27, 7.35) * mm], "startDerivative": vector(-0.06, -0.02) * mm, "endDerivative": vector(-0.15, 0.02) * mm});
            skFitSpline(sketch, "E208", {"points": [v(-0.8, 7.39) * mm, v(-0.86, 7.41) * mm, v(-0.91, 7.48) * mm], "startDerivative": vector(-0.12, 0.05) * mm, "endDerivative": vector(-0.1, 0.13) * mm});
            skFitSpline(sketch, "E209", {"points": [v(-8.87, 13.2) * mm, v(-8.8, 13.28) * mm, v(-8.68, 13.32) * mm, v(-8.59, 13.33) * mm], "startDerivative": vector(0.18, 0.27) * mm, "endDerivative": vector(0.29, 0) * mm});
            skFitSpline(sketch, "E210", {"points": [v(1.18, 13.2) * mm, v(1.15, 13.28) * mm, v(1.13, 13.33) * mm], "startDerivative": vector(-0.05, 0.15) * mm, "endDerivative": vector(-0.04, 0.1) * mm});
            skFitSpline(sketch, "E211", {"points": [v(3.7, 8.58) * mm, v(3.72, 8.52) * mm, v(3.72, 8.45) * mm, v(3.7, 8.4) * mm, v(3.67, 8.37) * mm, v(3.59, 8.32) * mm], "startDerivative": vector(0.07, -0.32) * mm, "endDerivative": vector(-0.37, -0.23) * mm});
            skFitSpline(sketch, "E212", {"points": [v(2.39, 8.75) * mm, v(2.43, 8.78) * mm, v(2.45, 8.82) * mm, v(2.45, 8.86) * mm, v(2.43, 8.95) * mm], "startDerivative": vector(0.2, 0.13) * mm, "endDerivative": vector(-0.1, 0.32) * mm});
            skFitSpline(sketch, "E213", {"points": [v(-5.71, 3.28) * mm, v(-5.77, 3.28) * mm, v(-5.83, 3.29) * mm, v(-5.86, 3.31) * mm, v(-5.9, 3.35) * mm, v(-5.9, 3.38) * mm, v(-5.9, 3.43) * mm, v(-5.9, 3.46) * mm, v(-5.9, 3.48) * mm], "startDerivative": vector(-0.4, 0) * mm, "endDerivative": vector(0.04, 0.24) * mm});
            skFitSpline(sketch, "E214", {"points": [v(-3.4, 3.4) * mm, v(-3.41, 3.4) * mm, v(-3.42, 3.42) * mm, v(-3.43, 3.43) * mm, v(-3.45, 3.44) * mm, v(-3.47, 3.44) * mm, v(-3.52, 3.44) * mm], "startDerivative": vector(-0.02, 0.12) * mm, "endDerivative": vector(-0.22, -0.02) * mm});
            skFitSpline(sketch, "E215", {"points": [v(-3.42, 2.63) * mm, v(-3.42, 2.65) * mm, v(-3.42, 2.7) * mm], "startDerivative": vector(-0.02, 0.05) * mm, "endDerivative": vector(0, 0.08) * mm});
            skFitSpline(sketch, "E216", {"points": [v(-0.63, -0.9) * mm, v(-0.65, -0.93) * mm, v(-0.7, -0.92) * mm, v(-0.73, -0.9) * mm, v(-0.76, -0.86) * mm], "startDerivative": vector(-0.1, -0.1) * mm, "endDerivative": vector(-0.12, 0.19) * mm});
            skFitSpline(sketch, "E217", {"points": [v(-8.87, -4.03) * mm, v(-8.87, -4.06) * mm, v(-8.86, -4.1) * mm, v(-8.83, -4.14) * mm, v(-8.8, -4.16) * mm, v(-8.77, -4.17) * mm, v(-8.75, -4.17) * mm], "startDerivative": vector(-0.01, -0.18) * mm, "endDerivative": vector(0.15, 0.01) * mm});
            skFitSpline(sketch, "E218", {"points": [v(7.58, -4.09) * mm, v(7.57, -4.15) * mm, v(7.5, -4.17) * mm], "startDerivative": vector(-0.01, -0.15) * mm, "endDerivative": vector(-0.16, -0.02) * mm});
            skFitSpline(sketch, "E219", {"points": [v(7.58, 2.37) * mm, v(7.58, 2.46) * mm, v(7.54, 2.56) * mm], "startDerivative": vector(0.02, 0.2) * mm, "endDerivative": vector(-0.1, 0.2) * mm});
            skFitSpline(sketch, "E220", {"points": [v(-6.36, 8.56) * mm, v(-6.41, 8.7) * mm, v(-6.36, 8.84) * mm], "startDerivative": vector(-0.15, 0.28) * mm, "endDerivative": vector(0.15, 0.27) * mm});
            skFitSpline(sketch, "E221", {"points": [v(-3.24, 10.14) * mm, v(-3.15, 10.16) * mm, v(-3.08, 10.14) * mm], "startDerivative": vector(0.18, 0.06) * mm, "endDerivative": vector(0.15, -0.07) * mm});
            skLineSegment(sketch, "E222", {"start": v(-10.25, -6.76) * mm, "end": v(-10.33, -7.57) * mm});
            skLineSegment(sketch, "E223", {"start": v(-10.33, -7.57) * mm, "end": v(-11.73, -7.43) * mm});
            skLineSegment(sketch, "E224", {"start": v(-11.73, -7.43) * mm, "end": v(-11.93, -8.86) * mm});
            skLineSegment(sketch, "E225", {"start": v(-11.93, -8.86) * mm, "end": v(-10.65, -9.04) * mm});
            skLineSegment(sketch, "E226", {"start": v(-10.65, -9.04) * mm, "end": v(-10.7, -9.62) * mm});
            skLineSegment(sketch, "E227", {"start": v(-10.7, -9.62) * mm, "end": v(-11.98, -9.52) * mm});
            skLineSegment(sketch, "E228", {"start": v(-11.98, -9.52) * mm, "end": v(-12.13, -11.24) * mm});
            skLineSegment(sketch, "E229", {"start": v(-12.13, -11.24) * mm, "end": v(-10.64, -11.37) * mm});
            skLineSegment(sketch, "E230", {"start": v(-10.64, -11.37) * mm, "end": v(-10.64, -11.96) * mm});
            skLineSegment(sketch, "E231", {"start": v(-10.64, -11.96) * mm, "end": v(-13.96, -11.72) * mm});
            skLineSegment(sketch, "E232", {"start": v(-13.96, -11.72) * mm, "end": v(-13.57, -6.37) * mm});
            skLineSegment(sketch, "E233", {"start": v(-13.57, -6.37) * mm, "end": v(-10.25, -6.76) * mm});
            skLineSegment(sketch, "E234", {"start": v(-9.22, -5.37) * mm, "end": v(-7.27, -5.6) * mm});
            skLineSegment(sketch, "E235", {"start": v(-7.27, -5.6) * mm, "end": v(-8.45, -10.95) * mm});
            skLineSegment(sketch, "E236", {"start": v(-8.45, -10.95) * mm, "end": v(-10.01, -10.57) * mm});
            skLineSegment(sketch, "E237", {"start": v(-10.01, -10.57) * mm, "end": v(-9.22, -5.37) * mm});
            skLineSegment(sketch, "E238", {"start": v(-3.9, -7.75) * mm, "end": v(-3.93, -8.72) * mm});
            skLineSegment(sketch, "E239", {"start": v(-3.93, -8.72) * mm, "end": v(-4.6, -8.72) * mm});
            skFitSpline(sketch, "E240", {"points": [v(-4.93, -7.85) * mm, v(-4.88, -7.69) * mm, v(-4.75, -7.53) * mm, v(-4.57, -7.44) * mm, v(-4.32, -7.45) * mm, v(-4.1, -7.52) * mm, v(-3.98, -7.63) * mm, v(-3.9, -7.75) * mm], "startDerivative": vector(0.24, 1.24) * mm, "endDerivative": vector(0.53, -0.96) * mm});
            skLineSegment(sketch, "E241", {"start": v(-2.11, -9.53) * mm, "end": v(-4.66, -9.2) * mm});
            skLineSegment(sketch, "E242", {"start": v(-3.79, -9.92) * mm, "end": v(-2.3, -10.11) * mm});
            skFitSpline(sketch, "E243", {"points": [v(-2.3, -10.11) * mm, v(-2.34, -10.38) * mm, v(-2.41, -10.6) * mm, v(-2.5, -10.82) * mm, v(-2.64, -11.02) * mm, v(-2.82, -11.21) * mm, v(-3.09, -11.37) * mm, v(-3.45, -11.46) * mm, v(-3.9, -11.51) * mm, v(-4.43, -11.51) * mm, v(-5, -11.5) * mm, v(-5.5, -11.43) * mm, v(-5.98, -11.26) * mm, v(-6.24, -11.1) * mm, v(-6.48, -10.9) * mm, v(-6.67, -10.57) * mm, v(-6.82, -10.11) * mm, v(-6.88, -9.54) * mm, v(-6.85, -9) * mm, v(-6.65, -8.16) * mm, v(-6.42, -7.74) * mm, v(-6.1, -7.44) * mm, v(-5.69, -7.21) * mm, v(-5.16, -7.05) * mm, v(-4.46, -7) * mm, v(-3.7, -7.1) * mm, v(-3.06, -7.3) * mm, v(-2.6, -7.6) * mm, v(-2.3, -7.93) * mm, v(-2.14, -8.3) * mm, v(-2.09, -8.64) * mm, v(-2.07, -9.03) * mm, v(-2.11, -9.53) * mm], "startDerivative": vector(-0.95, -11.32) * mm, "endDerivative": vector(-1.59, -15.64) * mm});
            skLineSegment(sketch, "E244", {"start": v(0.9, -11.07) * mm, "end": v(-0.73, -11.42) * mm});
            skLineSegment(sketch, "E245", {"start": v(-0.73, -11.42) * mm, "end": v(-1.9, -6.05) * mm});
            skLineSegment(sketch, "E246", {"start": v(-1.9, -6.05) * mm, "end": v(1.57, -5.55) * mm});
            skLineSegment(sketch, "E247", {"start": v(1.57, -5.55) * mm, "end": v(1.68, -6.35) * mm});
            skLineSegment(sketch, "E248", {"start": v(1.68, -6.35) * mm, "end": v(0.19, -6.64) * mm});
            skLineSegment(sketch, "E249", {"start": v(0.19, -6.64) * mm, "end": v(0.4, -8.1) * mm});
            skLineSegment(sketch, "E250", {"start": v(0.4, -8.1) * mm, "end": v(1.7, -7.9) * mm});
            skLineSegment(sketch, "E251", {"start": v(1.7, -7.9) * mm, "end": v(1.79, -8.46) * mm});
            skLineSegment(sketch, "E252", {"start": v(1.79, -8.46) * mm, "end": v(0.55, -8.7) * mm});
            skLineSegment(sketch, "E253", {"start": v(0.55, -8.7) * mm, "end": v(0.9, -11.07) * mm});
            skLineSegment(sketch, "E254", {"start": v(7.25, -11.07) * mm, "end": v(5.47, -11.4) * mm});
            skLineSegment(sketch, "E255", {"start": v(5.47, -11.4) * mm, "end": v(5.4, -11.18) * mm});
            skLineSegment(sketch, "E256", {"start": v(7.25, -11.07) * mm, "end": v(6.61, -6.64) * mm});
            skLineSegment(sketch, "E257", {"start": v(6.61, -6.64) * mm, "end": v(4.67, -7.06) * mm});
            skLineSegment(sketch, "E258", {"start": v(4.67, -7.06) * mm, "end": v(5.34, -10.47) * mm});
            skLineSegment(sketch, "E259", {"start": v(4.29, -10.8) * mm, "end": v(3.64, -7.43) * mm});
            skLineSegment(sketch, "E260", {"start": v(3.64, -7.43) * mm, "end": v(2.04, -7.65) * mm});
            skLineSegment(sketch, "E261", {"start": v(2.04, -7.65) * mm, "end": v(2.67, -11.2) * mm});
            skFitSpline(sketch, "E262", {"points": [v(2.67, -11.2) * mm, v(2.75, -11.41) * mm, v(2.94, -11.59) * mm, v(3.2, -11.7) * mm, v(3.53, -11.73) * mm, v(3.96, -11.7) * mm, v(4.34, -11.63) * mm, v(4.65, -11.51) * mm, v(4.94, -11.38) * mm, v(5.14, -11.29) * mm, v(5.27, -11.2) * mm, v(5.4, -11.18) * mm], "startDerivative": vector(0.77, -2.56) * mm, "endDerivative": vector(2.11, 0.24) * mm});
            skFitSpline(sketch, "E263", {"points": [v(5.34, -10.47) * mm, v(5.34, -10.62) * mm, v(5.25, -10.75) * mm, v(5.13, -10.86) * mm, v(4.94, -10.96) * mm, v(4.78, -11) * mm, v(4.6, -11.01) * mm, v(4.48, -10.98) * mm, v(4.38, -10.93) * mm, v(4.29, -10.8) * mm], "startDerivative": vector(0.2, -1.45) * mm, "endDerivative": vector(-0.8, 1.2) * mm});
            skLineSegment(sketch, "E264", {"start": v(9.82, -10.84) * mm, "end": v(8.22, -11.14) * mm});
            skLineSegment(sketch, "E265", {"start": v(8.22, -11.14) * mm, "end": v(7.37, -6.92) * mm});
            skLineSegment(sketch, "E266", {"start": v(7.37, -6.92) * mm, "end": v(9.29, -6.44) * mm});
            skLineSegment(sketch, "E267", {"start": v(9.29, -6.44) * mm, "end": v(9.32, -6.75) * mm});
            skLineSegment(sketch, "E268", {"start": v(9.25, -7.48) * mm, "end": v(9.82, -10.84) * mm});
            skLineSegment(sketch, "E269", {"start": v(10.93, -10.62) * mm, "end": v(10.33, -7.25) * mm});
            skLineSegment(sketch, "E270", {"start": v(10.93, -10.62) * mm, "end": v(12.65, -10.42) * mm});
            skLineSegment(sketch, "E271", {"start": v(12.65, -10.42) * mm, "end": v(12.02, -6.68) * mm});
            skPoint(sketch, "E272.1.internal.snap0", {"position": v(9.3, -6.6) * mm});
            skFitSpline(sketch, "E272", {"points": [v(9.25, -7.48) * mm, v(9.3, -7.3) * mm, v(9.42, -7.13) * mm, v(9.61, -7.01) * mm, v(9.85, -6.97) * mm, v(10.08, -7) * mm, v(10.19, -7.05) * mm, v(10.28, -7.12) * mm, v(10.33, -7.25) * mm], "startDerivative": vector(0.35, 1.5) * mm, "endDerivative": vector(0.4, -1.27) * mm});
            skFitSpline(sketch, "E273", {"points": [v(9.32, -6.75) * mm, v(9.5, -6.58) * mm, v(9.66, -6.45) * mm, v(9.97, -6.32) * mm, v(10.36, -6.2) * mm, v(10.78, -6.14) * mm, v(11.18, -6.15) * mm, v(11.53, -6.2) * mm, v(11.77, -6.3) * mm, v(11.91, -6.45) * mm, v(11.97, -6.56) * mm, v(12.02, -6.68) * mm], "startDerivative": vector(2, 2.1) * mm, "endDerivative": vector(0.8, -1.94) * mm});
            skFitSpline(sketch, "E274", {"points": [v(-4.84, -9.19) * mm, v(-4.93, -9.36) * mm, v(-5, -9.6) * mm, v(-5.08, -9.9) * mm, v(-5.1, -10.17) * mm, v(-5.11, -10.48) * mm, v(-5.05, -10.8) * mm, v(-4.87, -11.01) * mm, v(-4.65, -11.13) * mm, v(-4.42, -11.14) * mm, v(-4.23, -11.05) * mm, v(-4.09, -10.9) * mm, v(-3.96, -10.68) * mm, v(-3.87, -10.45) * mm, v(-3.82, -10.23) * mm, v(-3.79, -9.92) * mm], "startDerivative": vector(-1.74, -2.77) * mm, "endDerivative": vector(0.4, 4.42) * mm});
            skFitSpline(sketch, "E275", {"points": [v(-0.28, 4.7) * mm, v(-0.3, 4.78) * mm, v(-0.28, 4.87) * mm, v(-0.19, 4.94) * mm], "startDerivative": vector(-0.1, 0.25) * mm, "endDerivative": vector(0.3, 0.19) * mm});
            skLineSegment(sketch, "E276", {"start": v(8.16, 17.68) * mm, "end": v(14.27, 11.57) * mm, "construction": true});
            skCircle(sketch, "E277", {"center": v(11.21, 14.63) * mm, "radius": 1.5 * mm});
            skLineSegment(sketch, "E278.bottom", {"start": v(-13.73, 18.68) * mm, "end": v(12.27, 18.68) * mm});
            skLineSegment(sketch, "E278.top", {"start": v(-13.73, -13.32) * mm, "end": v(12.27, -13.32) * mm});
            skLineSegment(sketch, "E278.left", {"start": v(-16.73, 15.68) * mm, "end": v(-16.73, -10.32) * mm});
            skLineSegment(sketch, "E278.right", {"start": v(15.27, 15.68) * mm, "end": v(15.27, -10.32) * mm});
            skLineSegment(sketch, "E279", {"start": v(-16.73, 2.68) * mm, "end": v(15.27, 2.68) * mm, "construction": true});
            skLineSegment(sketch, "E280", {"start": v(-0.73, 18.68) * mm, "end": v(-0.73, -13.32) * mm, "construction": true});
            skLineSegment(sketch, "E281", {"start": v(-0.73, 2.68) * mm, "end": v(-0.73, -13.32) * mm, "construction": true});
            skLineSegment(sketch, "E282", {"start": v(-0.73, -13.32) * mm, "end": v(-0.73, 2.68) * mm, "construction": true});
            skLineSegment(sketch, "E283", {"start": v(-0.73, 18.68) * mm, "end": v(-0.73, 2.68) * mm, "construction": true});
            skPoint(sketch, "E284.visualSharp", {"position": v(-16.73, 18.68) * mm});
            skArc(sketch, "E284.filletArc", {"start": v(-13.73, 18.68) * mm, "mid": v(-15.85, 17.8) * mm, "end": v(-16.73, 15.68) * mm});
            skPoint(sketch, "E285.visualSharp", {"position": v(15.27, 18.68) * mm});
            skArc(sketch, "E285.filletArc", {"start": v(15.27, 15.68) * mm, "mid": v(14.39, 17.8) * mm, "end": v(12.27, 18.68) * mm});
            skPoint(sketch, "E286.visualSharp", {"position": v(15.27, -13.32) * mm});
            skArc(sketch, "E286.filletArc", {"start": v(12.27, -13.32) * mm, "mid": v(14.39, -12.44) * mm, "end": v(15.27, -10.32) * mm});
            skPoint(sketch, "E287.visualSharp", {"position": v(-16.73, -13.32) * mm});
            skArc(sketch, "E287.filletArc", {"start": v(-16.73, -10.32) * mm, "mid": v(-15.85, -12.44) * mm, "end": v(-13.73, -13.32) * mm});
            skLineSegment(sketch, "E288", {"start": v(-4.92, -7.8) * mm, "end": v(-5.1, -10.17) * mm});
            skLineSegment(sketch, "E289", {"start": v(-4.6, -8.72) * mm, "end": v(-4.66, -9.2) * mm});
            skSolve(sketch);
        }
        {
            var Q0;
            Q0 = qSketchRegion(id + "F3", true);
            var Q1;
            {var subQ0=sQuery(id+"F3.wireOp",EDGE,"E277");var subQ1=makeQuery(id+"F1.opExtrude","CAP_EDGE",EDGE,{"disambiguationData":[OSD([sQuery(id+"F0.wireOp",EDGE,"E133.top")])],"isStart":false});var subQ2=makeQuery(id+"F3.imprint","INTERSECT",VERTEX,{"disambiguationData":[OD(0.0)],"derivedFrom":[subQ1,subQ0]});Q1=makeQuery(id+"F3.imprint","IMPRINT",FACE,{"disambiguationData":[TD([[makeQuery(id+"F3.imprint","IMPRINT",EDGE,{"disambiguationData":[TD([[subQ2,1.0]])],"derivedFrom":subQ0}),1.0]])]});}
            var Q2;
            {var subQ0=sQuery(id+"F3.wireOp",EDGE,"E277");var subQ1=makeQuery(id+"F1.opExtrude","CAP_EDGE",EDGE,{"disambiguationData":[OSD([sQuery(id+"F0.wireOp",EDGE,"E133.top")])],"isStart":false});var subQ2=makeQuery(id+"F3.imprint","INTERSECT",VERTEX,{"disambiguationData":[OD(0.0)],"derivedFrom":[subQ1,subQ0]});Q2=makeQuery(id+"F3.imprint","IMPRINT",FACE,{"disambiguationData":[TD([[makeQuery(id+"F3.imprint","IMPRINT",EDGE,{"disambiguationData":[TD([[subQ2,-1.0]])],"derivedFrom":subQ0}),1.0]])]});}
            extrude(context, id + "F4", {"entities" : qUnion([Q0, Q1, Q2]), "depth" : 1 * mm});
        }
        {
            var Q0;
            Q0=makeQuery(id+"F4.opExtrude","SWEPT_BODY",BODY,{"disambiguationData":[OSD([sQuery(id+"F3.wireOp",EDGE,"E148"),sQuery(id+"F3.wireOp",EDGE,"E149"),sQuery(id+"F3.wireOp",EDGE,"E150"),sQuery(id+"F3.wireOp",EDGE,"E151"),sQuery(id+"F3.wireOp",EDGE,"E152"),sQuery(id+"F3.wireOp",EDGE,"E153"),sQuery(id+"F3.wireOp",EDGE,"E154"),sQuery(id+"F3.wireOp",EDGE,"E155"),sQuery(id+"F3.wireOp",EDGE,"E156"),sQuery(id+"F3.wireOp",EDGE,"E157"),sQuery(id+"F3.wireOp",EDGE,"E158"),sQuery(id+"F3.wireOp",EDGE,"E159"),sQuery(id+"F3.wireOp",EDGE,"E160"),sQuery(id+"F3.wireOp",EDGE,"E161"),sQuery(id+"F3.wireOp",EDGE,"E162"),sQuery(id+"F3.wireOp",EDGE,"E163"),sQuery(id+"F3.wireOp",EDGE,"E164"),sQuery(id+"F3.wireOp",EDGE,"E165"),sQuery(id+"F3.wireOp",EDGE,"E166"),sQuery(id+"F3.wireOp",EDGE,"E167"),sQuery(id+"F3.wireOp",EDGE,"E168"),sQuery(id+"F3.wireOp",EDGE,"E169"),sQuery(id+"F3.wireOp",EDGE,"E170"),sQuery(id+"F3.wireOp",EDGE,"E171"),sQuery(id+"F3.wireOp",EDGE,"E172"),sQuery(id+"F3.wireOp",EDGE,"E173"),sQuery(id+"F3.wireOp",EDGE,"E174"),sQuery(id+"F3.wireOp",EDGE,"E175"),sQuery(id+"F3.wireOp",EDGE,"E176"),sQuery(id+"F3.wireOp",EDGE,"E177"),sQuery(id+"F3.wireOp",EDGE,"E178"),sQuery(id+"F3.wireOp",EDGE,"E179"),sQuery(id+"F3.wireOp",EDGE,"E180"),sQuery(id+"F3.wireOp",EDGE,"E181"),sQuery(id+"F3.wireOp",EDGE,"E182"),sQuery(id+"F3.wireOp",EDGE,"E183"),sQuery(id+"F3.wireOp",EDGE,"E184"),sQuery(id+"F3.wireOp",EDGE,"E185"),sQuery(id+"F3.wireOp",EDGE,"E186"),sQuery(id+"F3.wireOp",EDGE,"E187"),sQuery(id+"F3.wireOp",EDGE,"E188"),sQuery(id+"F3.wireOp",EDGE,"E189"),sQuery(id+"F3.wireOp",EDGE,"E190"),sQuery(id+"F3.wireOp",EDGE,"E191"),sQuery(id+"F3.wireOp",EDGE,"E192"),sQuery(id+"F3.wireOp",EDGE,"E193"),sQuery(id+"F3.wireOp",EDGE,"E194"),sQuery(id+"F3.wireOp",EDGE,"E195"),sQuery(id+"F3.wireOp",EDGE,"E196"),sQuery(id+"F3.wireOp",EDGE,"E197"),sQuery(id+"F3.wireOp",EDGE,"E198"),sQuery(id+"F3.wireOp",EDGE,"E199"),sQuery(id+"F3.wireOp",EDGE,"E200"),sQuery(id+"F3.wireOp",EDGE,"E201"),sQuery(id+"F3.wireOp",EDGE,"E202"),sQuery(id+"F3.wireOp",EDGE,"E203"),sQuery(id+"F3.wireOp",EDGE,"E204"),sQuery(id+"F3.wireOp",EDGE,"E205"),sQuery(id+"F3.wireOp",EDGE,"E206"),sQuery(id+"F3.wireOp",EDGE,"E207"),sQuery(id+"F3.wireOp",EDGE,"E208"),sQuery(id+"F3.wireOp",EDGE,"E209"),sQuery(id+"F3.wireOp",EDGE,"E210"),sQuery(id+"F3.wireOp",EDGE,"E211"),sQuery(id+"F3.wireOp",EDGE,"E212"),sQuery(id+"F3.wireOp",EDGE,"E213"),sQuery(id+"F3.wireOp",EDGE,"E214"),sQuery(id+"F3.wireOp",EDGE,"E215"),sQuery(id+"F3.wireOp",EDGE,"E216"),sQuery(id+"F3.wireOp",EDGE,"E217"),sQuery(id+"F3.wireOp",EDGE,"E218"),sQuery(id+"F3.wireOp",EDGE,"E219"),sQuery(id+"F3.wireOp",EDGE,"E220"),sQuery(id+"F3.wireOp",EDGE,"E221"),sQuery(id+"F3.wireOp",EDGE,"E222"),sQuery(id+"F3.wireOp",EDGE,"E223"),sQuery(id+"F3.wireOp",EDGE,"E224"),sQuery(id+"F3.wireOp",EDGE,"E225"),sQuery(id+"F3.wireOp",EDGE,"E226"),sQuery(id+"F3.wireOp",EDGE,"E227"),sQuery(id+"F3.wireOp",EDGE,"E228"),sQuery(id+"F3.wireOp",EDGE,"E229"),sQuery(id+"F3.wireOp",EDGE,"E230"),sQuery(id+"F3.wireOp",EDGE,"E231"),sQuery(id+"F3.wireOp",EDGE,"E232"),sQuery(id+"F3.wireOp",EDGE,"E233"),sQuery(id+"F3.wireOp",EDGE,"E234"),sQuery(id+"F3.wireOp",EDGE,"E235"),sQuery(id+"F3.wireOp",EDGE,"E236"),sQuery(id+"F3.wireOp",EDGE,"E237"),sQuery(id+"F3.wireOp",EDGE,"E238"),sQuery(id+"F3.wireOp",EDGE,"E239"),sQuery(id+"F3.wireOp",EDGE,"E240"),sQuery(id+"F3.wireOp",EDGE,"E241"),sQuery(id+"F3.wireOp",EDGE,"E242"),sQuery(id+"F3.wireOp",EDGE,"E243"),sQuery(id+"F3.wireOp",EDGE,"E244"),sQuery(id+"F3.wireOp",EDGE,"E245"),sQuery(id+"F3.wireOp",EDGE,"E246"),sQuery(id+"F3.wireOp",EDGE,"E247"),sQuery(id+"F3.wireOp",EDGE,"E248"),sQuery(id+"F3.wireOp",EDGE,"E249"),sQuery(id+"F3.wireOp",EDGE,"E250"),sQuery(id+"F3.wireOp",EDGE,"E251"),sQuery(id+"F3.wireOp",EDGE,"E252"),sQuery(id+"F3.wireOp",EDGE,"E253"),sQuery(id+"F3.wireOp",EDGE,"E254"),sQuery(id+"F3.wireOp",EDGE,"E255"),sQuery(id+"F3.wireOp",EDGE,"E256"),sQuery(id+"F3.wireOp",EDGE,"E257"),sQuery(id+"F3.wireOp",EDGE,"E258"),sQuery(id+"F3.wireOp",EDGE,"E259"),sQuery(id+"F3.wireOp",EDGE,"E260"),sQuery(id+"F3.wireOp",EDGE,"E261"),sQuery(id+"F3.wireOp",EDGE,"E262"),sQuery(id+"F3.wireOp",EDGE,"E263"),sQuery(id+"F3.wireOp",EDGE,"E264"),sQuery(id+"F3.wireOp",EDGE,"E265"),sQuery(id+"F3.wireOp",EDGE,"E266"),sQuery(id+"F3.wireOp",EDGE,"E267"),sQuery(id+"F3.wireOp",EDGE,"E268"),sQuery(id+"F3.wireOp",EDGE,"E269"),sQuery(id+"F3.wireOp",EDGE,"E270"),sQuery(id+"F3.wireOp",EDGE,"E271"),sQuery(id+"F3.wireOp",EDGE,"E272"),sQuery(id+"F3.wireOp",EDGE,"E273"),sQuery(id+"F3.wireOp",EDGE,"E274"),sQuery(id+"F3.wireOp",EDGE,"E275"),sQuery(id+"F3.wireOp",EDGE,"E278.bottom"),sQuery(id+"F3.wireOp",EDGE,"E278.top"),sQuery(id+"F3.wireOp",EDGE,"E278.left"),sQuery(id+"F3.wireOp",EDGE,"E278.right"),sQuery(id+"F3.wireOp",EDGE,"E284.filletArc"),sQuery(id+"F3.wireOp",EDGE,"E285.filletArc"),sQuery(id+"F3.wireOp",EDGE,"E286.filletArc"),sQuery(id+"F3.wireOp",EDGE,"E287.filletArc"),sQuery(id+"F3.wireOp",EDGE,"E288"),sQuery(id+"F3.wireOp",EDGE,"E289")])]});
            var Q1;
            Q1=makeQuery(id+"F4.opExtrude","SWEPT_EDGE",EDGE,{"disambiguationData":[OSD([sQuery(id+"F3.wireOp",EDGE,"E278.top"),sQuery(id+"F3.wireOp",EDGE,"E286.filletArc")])]});
            transform(context, id + "F5", {"entities" : qUnion([Q0]), "transformType" : TransformType.ROTATION, "transformAxis" : qUnion([Q1]), "angle" : 180 * degree, "oppositeDirection" : true, "makeCopy" : false});
        }
        {
            var Q0;
            Q0=makeQuery(id+"F4.opExtrude","CAP_EDGE",EDGE,{"disambiguationData":[OSD([sQuery(id+"F3.wireOp",EDGE,"E286.filletArc")])],"isStart":true});
            cPoint(context, id + "F6", {"entities" : qUnion([Q0]), "parameter" : 0.5});
        }
        {
            var Q0;
            Q0=makeQuery(id+"F1.opExtrude","CAP_EDGE",EDGE,{"disambiguationData":[OSD([sQuery(id+"F0.wireOp",EDGE,"E142.filletArc")])],"isStart":false});
            cPoint(context, id + "F7", {"entities" : qUnion([Q0]), "parameter" : 0.5});
        }
        {
            var Q0;
            Q0=makeQuery(id+"F4.opExtrude","SWEPT_BODY",BODY,{"disambiguationData":[OSD([sQuery(id+"F3.wireOp",EDGE,"E148"),sQuery(id+"F3.wireOp",EDGE,"E149"),sQuery(id+"F3.wireOp",EDGE,"E150"),sQuery(id+"F3.wireOp",EDGE,"E151"),sQuery(id+"F3.wireOp",EDGE,"E152"),sQuery(id+"F3.wireOp",EDGE,"E153"),sQuery(id+"F3.wireOp",EDGE,"E154"),sQuery(id+"F3.wireOp",EDGE,"E155"),sQuery(id+"F3.wireOp",EDGE,"E156"),sQuery(id+"F3.wireOp",EDGE,"E157"),sQuery(id+"F3.wireOp",EDGE,"E158"),sQuery(id+"F3.wireOp",EDGE,"E159"),sQuery(id+"F3.wireOp",EDGE,"E160"),sQuery(id+"F3.wireOp",EDGE,"E161"),sQuery(id+"F3.wireOp",EDGE,"E162"),sQuery(id+"F3.wireOp",EDGE,"E163"),sQuery(id+"F3.wireOp",EDGE,"E164"),sQuery(id+"F3.wireOp",EDGE,"E165"),sQuery(id+"F3.wireOp",EDGE,"E166"),sQuery(id+"F3.wireOp",EDGE,"E167"),sQuery(id+"F3.wireOp",EDGE,"E168"),sQuery(id+"F3.wireOp",EDGE,"E169"),sQuery(id+"F3.wireOp",EDGE,"E170"),sQuery(id+"F3.wireOp",EDGE,"E171"),sQuery(id+"F3.wireOp",EDGE,"E172"),sQuery(id+"F3.wireOp",EDGE,"E173"),sQuery(id+"F3.wireOp",EDGE,"E174"),sQuery(id+"F3.wireOp",EDGE,"E175"),sQuery(id+"F3.wireOp",EDGE,"E176"),sQuery(id+"F3.wireOp",EDGE,"E177"),sQuery(id+"F3.wireOp",EDGE,"E178"),sQuery(id+"F3.wireOp",EDGE,"E179"),sQuery(id+"F3.wireOp",EDGE,"E180"),sQuery(id+"F3.wireOp",EDGE,"E181"),sQuery(id+"F3.wireOp",EDGE,"E182"),sQuery(id+"F3.wireOp",EDGE,"E183"),sQuery(id+"F3.wireOp",EDGE,"E184"),sQuery(id+"F3.wireOp",EDGE,"E185"),sQuery(id+"F3.wireOp",EDGE,"E186"),sQuery(id+"F3.wireOp",EDGE,"E187"),sQuery(id+"F3.wireOp",EDGE,"E188"),sQuery(id+"F3.wireOp",EDGE,"E189"),sQuery(id+"F3.wireOp",EDGE,"E190"),sQuery(id+"F3.wireOp",EDGE,"E191"),sQuery(id+"F3.wireOp",EDGE,"E192"),sQuery(id+"F3.wireOp",EDGE,"E193"),sQuery(id+"F3.wireOp",EDGE,"E194"),sQuery(id+"F3.wireOp",EDGE,"E195"),sQuery(id+"F3.wireOp",EDGE,"E196"),sQuery(id+"F3.wireOp",EDGE,"E197"),sQuery(id+"F3.wireOp",EDGE,"E198"),sQuery(id+"F3.wireOp",EDGE,"E199"),sQuery(id+"F3.wireOp",EDGE,"E200"),sQuery(id+"F3.wireOp",EDGE,"E201"),sQuery(id+"F3.wireOp",EDGE,"E202"),sQuery(id+"F3.wireOp",EDGE,"E203"),sQuery(id+"F3.wireOp",EDGE,"E204"),sQuery(id+"F3.wireOp",EDGE,"E205"),sQuery(id+"F3.wireOp",EDGE,"E206"),sQuery(id+"F3.wireOp",EDGE,"E207"),sQuery(id+"F3.wireOp",EDGE,"E208"),sQuery(id+"F3.wireOp",EDGE,"E209"),sQuery(id+"F3.wireOp",EDGE,"E210"),sQuery(id+"F3.wireOp",EDGE,"E211"),sQuery(id+"F3.wireOp",EDGE,"E212"),sQuery(id+"F3.wireOp",EDGE,"E213"),sQuery(id+"F3.wireOp",EDGE,"E214"),sQuery(id+"F3.wireOp",EDGE,"E215"),sQuery(id+"F3.wireOp",EDGE,"E216"),sQuery(id+"F3.wireOp",EDGE,"E217"),sQuery(id+"F3.wireOp",EDGE,"E218"),sQuery(id+"F3.wireOp",EDGE,"E219"),sQuery(id+"F3.wireOp",EDGE,"E220"),sQuery(id+"F3.wireOp",EDGE,"E221"),sQuery(id+"F3.wireOp",EDGE,"E222"),sQuery(id+"F3.wireOp",EDGE,"E223"),sQuery(id+"F3.wireOp",EDGE,"E224"),sQuery(id+"F3.wireOp",EDGE,"E225"),sQuery(id+"F3.wireOp",EDGE,"E226"),sQuery(id+"F3.wireOp",EDGE,"E227"),sQuery(id+"F3.wireOp",EDGE,"E228"),sQuery(id+"F3.wireOp",EDGE,"E229"),sQuery(id+"F3.wireOp",EDGE,"E230"),sQuery(id+"F3.wireOp",EDGE,"E231"),sQuery(id+"F3.wireOp",EDGE,"E232"),sQuery(id+"F3.wireOp",EDGE,"E233"),sQuery(id+"F3.wireOp",EDGE,"E234"),sQuery(id+"F3.wireOp",EDGE,"E235"),sQuery(id+"F3.wireOp",EDGE,"E236"),sQuery(id+"F3.wireOp",EDGE,"E237"),sQuery(id+"F3.wireOp",EDGE,"E238"),sQuery(id+"F3.wireOp",EDGE,"E239"),sQuery(id+"F3.wireOp",EDGE,"E240"),sQuery(id+"F3.wireOp",EDGE,"E241"),sQuery(id+"F3.wireOp",EDGE,"E242"),sQuery(id+"F3.wireOp",EDGE,"E243"),sQuery(id+"F3.wireOp",EDGE,"E244"),sQuery(id+"F3.wireOp",EDGE,"E245"),sQuery(id+"F3.wireOp",EDGE,"E246"),sQuery(id+"F3.wireOp",EDGE,"E247"),sQuery(id+"F3.wireOp",EDGE,"E248"),sQuery(id+"F3.wireOp",EDGE,"E249"),sQuery(id+"F3.wireOp",EDGE,"E250"),sQuery(id+"F3.wireOp",EDGE,"E251"),sQuery(id+"F3.wireOp",EDGE,"E252"),sQuery(id+"F3.wireOp",EDGE,"E253"),sQuery(id+"F3.wireOp",EDGE,"E254"),sQuery(id+"F3.wireOp",EDGE,"E255"),sQuery(id+"F3.wireOp",EDGE,"E256"),sQuery(id+"F3.wireOp",EDGE,"E257"),sQuery(id+"F3.wireOp",EDGE,"E258"),sQuery(id+"F3.wireOp",EDGE,"E259"),sQuery(id+"F3.wireOp",EDGE,"E260"),sQuery(id+"F3.wireOp",EDGE,"E261"),sQuery(id+"F3.wireOp",EDGE,"E262"),sQuery(id+"F3.wireOp",EDGE,"E263"),sQuery(id+"F3.wireOp",EDGE,"E264"),sQuery(id+"F3.wireOp",EDGE,"E265"),sQuery(id+"F3.wireOp",EDGE,"E266"),sQuery(id+"F3.wireOp",EDGE,"E267"),sQuery(id+"F3.wireOp",EDGE,"E268"),sQuery(id+"F3.wireOp",EDGE,"E269"),sQuery(id+"F3.wireOp",EDGE,"E270"),sQuery(id+"F3.wireOp",EDGE,"E271"),sQuery(id+"F3.wireOp",EDGE,"E272"),sQuery(id+"F3.wireOp",EDGE,"E273"),sQuery(id+"F3.wireOp",EDGE,"E274"),sQuery(id+"F3.wireOp",EDGE,"E275"),sQuery(id+"F3.wireOp",EDGE,"E278.bottom"),sQuery(id+"F3.wireOp",EDGE,"E278.top"),sQuery(id+"F3.wireOp",EDGE,"E278.left"),sQuery(id+"F3.wireOp",EDGE,"E278.right"),sQuery(id+"F3.wireOp",EDGE,"E284.filletArc"),sQuery(id+"F3.wireOp",EDGE,"E285.filletArc"),sQuery(id+"F3.wireOp",EDGE,"E286.filletArc"),sQuery(id+"F3.wireOp",EDGE,"E287.filletArc"),sQuery(id+"F3.wireOp",EDGE,"E288"),sQuery(id+"F3.wireOp",EDGE,"E289")])]});
            var Q1;
            Q1 = qCreatedBy(id + "F6" ,VERTEX);
            var Q2;
            Q2 = qCreatedBy(id + "F7" ,VERTEX);
            transform(context, id + "F8", {"entities" : qUnion([Q0]), "transformType" : TransformType.TRANSLATION_ENTITY, "oppositeDirectionEntity" : false, "transformLine" : qUnion([Q1, Q2]), "makeCopy" : false});
        }
        {
            var Q0;
            Q0=makeQuery(id+"F0.imprint","IMPRINT",FACE,{"disambiguationData":[TD([[makeQuery(id+"F0.imprint","IMPRINT",EDGE,{"derivedFrom":sQuery(id+"F0.wireOp",EDGE,"E132")}),1.0]])]});
            var Q1;
            Q1=sQuery(id+"F0.wireOp",EDGE,"E132");
            extrude(context, id + "F9", {"entities" : qUnion([Q0]), "operationType" : NewBodyOperationType.REMOVE, "surfaceEntities" : qUnion([Q1]), "endBound" : BoundingType.THROUGH_ALL, "oppositeDirection" : true, "depth" : 25 * mm});
        }
        {
            var Q0;
            Q0=makeQuery(id+"F2.opExtrude","CAP_EDGE",EDGE,{"disambiguationData":[OSD([sQuery(id+"F0.wireOp",EDGE,"E132")])],"isStart":false});
            var Q1;
            Q1=makeQuery(id+"F9.boolean.opBoolean","INTERSECT",EDGE,{"derivedFrom":[makeQuery(id+"F4.opExtrude","CAP_FACE",FACE,{"disambiguationData":[OSD([sQuery(id+"F3.wireOp",EDGE,"E148"),sQuery(id+"F3.wireOp",EDGE,"E149"),sQuery(id+"F3.wireOp",EDGE,"E150"),sQuery(id+"F3.wireOp",EDGE,"E151"),sQuery(id+"F3.wireOp",EDGE,"E152"),sQuery(id+"F3.wireOp",EDGE,"E153"),sQuery(id+"F3.wireOp",EDGE,"E154"),sQuery(id+"F3.wireOp",EDGE,"E155"),sQuery(id+"F3.wireOp",EDGE,"E156"),sQuery(id+"F3.wireOp",EDGE,"E157"),sQuery(id+"F3.wireOp",EDGE,"E158"),sQuery(id+"F3.wireOp",EDGE,"E159"),sQuery(id+"F3.wireOp",EDGE,"E160"),sQuery(id+"F3.wireOp",EDGE,"E161"),sQuery(id+"F3.wireOp",EDGE,"E162"),sQuery(id+"F3.wireOp",EDGE,"E163"),sQuery(id+"F3.wireOp",EDGE,"E164"),sQuery(id+"F3.wireOp",EDGE,"E165"),sQuery(id+"F3.wireOp",EDGE,"E166"),sQuery(id+"F3.wireOp",EDGE,"E167"),sQuery(id+"F3.wireOp",EDGE,"E168"),sQuery(id+"F3.wireOp",EDGE,"E169"),sQuery(id+"F3.wireOp",EDGE,"E170"),sQuery(id+"F3.wireOp",EDGE,"E171"),sQuery(id+"F3.wireOp",EDGE,"E172"),sQuery(id+"F3.wireOp",EDGE,"E173"),sQuery(id+"F3.wireOp",EDGE,"E174"),sQuery(id+"F3.wireOp",EDGE,"E175"),sQuery(id+"F3.wireOp",EDGE,"E176"),sQuery(id+"F3.wireOp",EDGE,"E177"),sQuery(id+"F3.wireOp",EDGE,"E178"),sQuery(id+"F3.wireOp",EDGE,"E179"),sQuery(id+"F3.wireOp",EDGE,"E180"),sQuery(id+"F3.wireOp",EDGE,"E181"),sQuery(id+"F3.wireOp",EDGE,"E182"),sQuery(id+"F3.wireOp",EDGE,"E183"),sQuery(id+"F3.wireOp",EDGE,"E184"),sQuery(id+"F3.wireOp",EDGE,"E185"),sQuery(id+"F3.wireOp",EDGE,"E186"),sQuery(id+"F3.wireOp",EDGE,"E187"),sQuery(id+"F3.wireOp",EDGE,"E188"),sQuery(id+"F3.wireOp",EDGE,"E189"),sQuery(id+"F3.wireOp",EDGE,"E190"),sQuery(id+"F3.wireOp",EDGE,"E191"),sQuery(id+"F3.wireOp",EDGE,"E192"),sQuery(id+"F3.wireOp",EDGE,"E193"),sQuery(id+"F3.wireOp",EDGE,"E194"),sQuery(id+"F3.wireOp",EDGE,"E195"),sQuery(id+"F3.wireOp",EDGE,"E196"),sQuery(id+"F3.wireOp",EDGE,"E197"),sQuery(id+"F3.wireOp",EDGE,"E198"),sQuery(id+"F3.wireOp",EDGE,"E199"),sQuery(id+"F3.wireOp",EDGE,"E200"),sQuery(id+"F3.wireOp",EDGE,"E201"),sQuery(id+"F3.wireOp",EDGE,"E202"),sQuery(id+"F3.wireOp",EDGE,"E203"),sQuery(id+"F3.wireOp",EDGE,"E204"),sQuery(id+"F3.wireOp",EDGE,"E205"),sQuery(id+"F3.wireOp",EDGE,"E206"),sQuery(id+"F3.wireOp",EDGE,"E207"),sQuery(id+"F3.wireOp",EDGE,"E208"),sQuery(id+"F3.wireOp",EDGE,"E209"),sQuery(id+"F3.wireOp",EDGE,"E210"),sQuery(id+"F3.wireOp",EDGE,"E211"),sQuery(id+"F3.wireOp",EDGE,"E212"),sQuery(id+"F3.wireOp",EDGE,"E213"),sQuery(id+"F3.wireOp",EDGE,"E214"),sQuery(id+"F3.wireOp",EDGE,"E215"),sQuery(id+"F3.wireOp",EDGE,"E216"),sQuery(id+"F3.wireOp",EDGE,"E217"),sQuery(id+"F3.wireOp",EDGE,"E218"),sQuery(id+"F3.wireOp",EDGE,"E219"),sQuery(id+"F3.wireOp",EDGE,"E220"),sQuery(id+"F3.wireOp",EDGE,"E221"),sQuery(id+"F3.wireOp",EDGE,"E222"),sQuery(id+"F3.wireOp",EDGE,"E223"),sQuery(id+"F3.wireOp",EDGE,"E224"),sQuery(id+"F3.wireOp",EDGE,"E225"),sQuery(id+"F3.wireOp",EDGE,"E226"),sQuery(id+"F3.wireOp",EDGE,"E227"),sQuery(id+"F3.wireOp",EDGE,"E228"),sQuery(id+"F3.wireOp",EDGE,"E229"),sQuery(id+"F3.wireOp",EDGE,"E230"),sQuery(id+"F3.wireOp",EDGE,"E231"),sQuery(id+"F3.wireOp",EDGE,"E232"),sQuery(id+"F3.wireOp",EDGE,"E233"),sQuery(id+"F3.wireOp",EDGE,"E234"),sQuery(id+"F3.wireOp",EDGE,"E235"),sQuery(id+"F3.wireOp",EDGE,"E236"),sQuery(id+"F3.wireOp",EDGE,"E237"),sQuery(id+"F3.wireOp",EDGE,"E238"),sQuery(id+"F3.wireOp",EDGE,"E239"),sQuery(id+"F3.wireOp",EDGE,"E240"),sQuery(id+"F3.wireOp",EDGE,"E241"),sQuery(id+"F3.wireOp",EDGE,"E242"),sQuery(id+"F3.wireOp",EDGE,"E243"),sQuery(id+"F3.wireOp",EDGE,"E244"),sQuery(id+"F3.wireOp",EDGE,"E245"),sQuery(id+"F3.wireOp",EDGE,"E246"),sQuery(id+"F3.wireOp",EDGE,"E247"),sQuery(id+"F3.wireOp",EDGE,"E248"),sQuery(id+"F3.wireOp",EDGE,"E249"),sQuery(id+"F3.wireOp",EDGE,"E250"),sQuery(id+"F3.wireOp",EDGE,"E251"),sQuery(id+"F3.wireOp",EDGE,"E252"),sQuery(id+"F3.wireOp",EDGE,"E253"),sQuery(id+"F3.wireOp",EDGE,"E254"),sQuery(id+"F3.wireOp",EDGE,"E255"),sQuery(id+"F3.wireOp",EDGE,"E256"),sQuery(id+"F3.wireOp",EDGE,"E257"),sQuery(id+"F3.wireOp",EDGE,"E258"),sQuery(id+"F3.wireOp",EDGE,"E259"),sQuery(id+"F3.wireOp",EDGE,"E260"),sQuery(id+"F3.wireOp",EDGE,"E261"),sQuery(id+"F3.wireOp",EDGE,"E262"),sQuery(id+"F3.wireOp",EDGE,"E263"),sQuery(id+"F3.wireOp",EDGE,"E264"),sQuery(id+"F3.wireOp",EDGE,"E265"),sQuery(id+"F3.wireOp",EDGE,"E266"),sQuery(id+"F3.wireOp",EDGE,"E267"),sQuery(id+"F3.wireOp",EDGE,"E268"),sQuery(id+"F3.wireOp",EDGE,"E269"),sQuery(id+"F3.wireOp",EDGE,"E270"),sQuery(id+"F3.wireOp",EDGE,"E271"),sQuery(id+"F3.wireOp",EDGE,"E272"),sQuery(id+"F3.wireOp",EDGE,"E273"),sQuery(id+"F3.wireOp",EDGE,"E274"),sQuery(id+"F3.wireOp",EDGE,"E275"),sQuery(id+"F3.wireOp",EDGE,"E278.bottom"),sQuery(id+"F3.wireOp",EDGE,"E278.top"),sQuery(id+"F3.wireOp",EDGE,"E278.left"),sQuery(id+"F3.wireOp",EDGE,"E278.right"),sQuery(id+"F3.wireOp",EDGE,"E284.filletArc"),sQuery(id+"F3.wireOp",EDGE,"E285.filletArc"),sQuery(id+"F3.wireOp",EDGE,"E286.filletArc"),sQuery(id+"F3.wireOp",EDGE,"E287.filletArc"),sQuery(id+"F3.wireOp",EDGE,"E288"),sQuery(id+"F3.wireOp",EDGE,"E289")])],"isStart":false}),makeQuery(id+"F9.opExtrude","SWEPT_FACE",FACE,{"disambiguationData":[OSD([sQuery(id+"F0.wireOp",EDGE,"E132")])]})]});
            var Q2;
            Q2=makeQuery(id+"F4.opExtrude","CAP_EDGE",EDGE,{"disambiguationData":[OSD([sQuery(id+"F3.wireOp",EDGE,"E278.bottom")])],"isStart":false});
            var Q3;
            Q3=makeQuery(id+"F2.opExtrude","CAP_EDGE",EDGE,{"disambiguationData":[OSD([sQuery(id+"F0.wireOp",EDGE,"E133.bottom")])],"isStart":false});
            fillet(context, id + "F10", {"entities" : qUnion([Q0, Q1, Q2, Q3]), "radius" : 1 * mm, "tangentPropagation" : true, "allowEdgeOverflow" : false});
        }
    });
